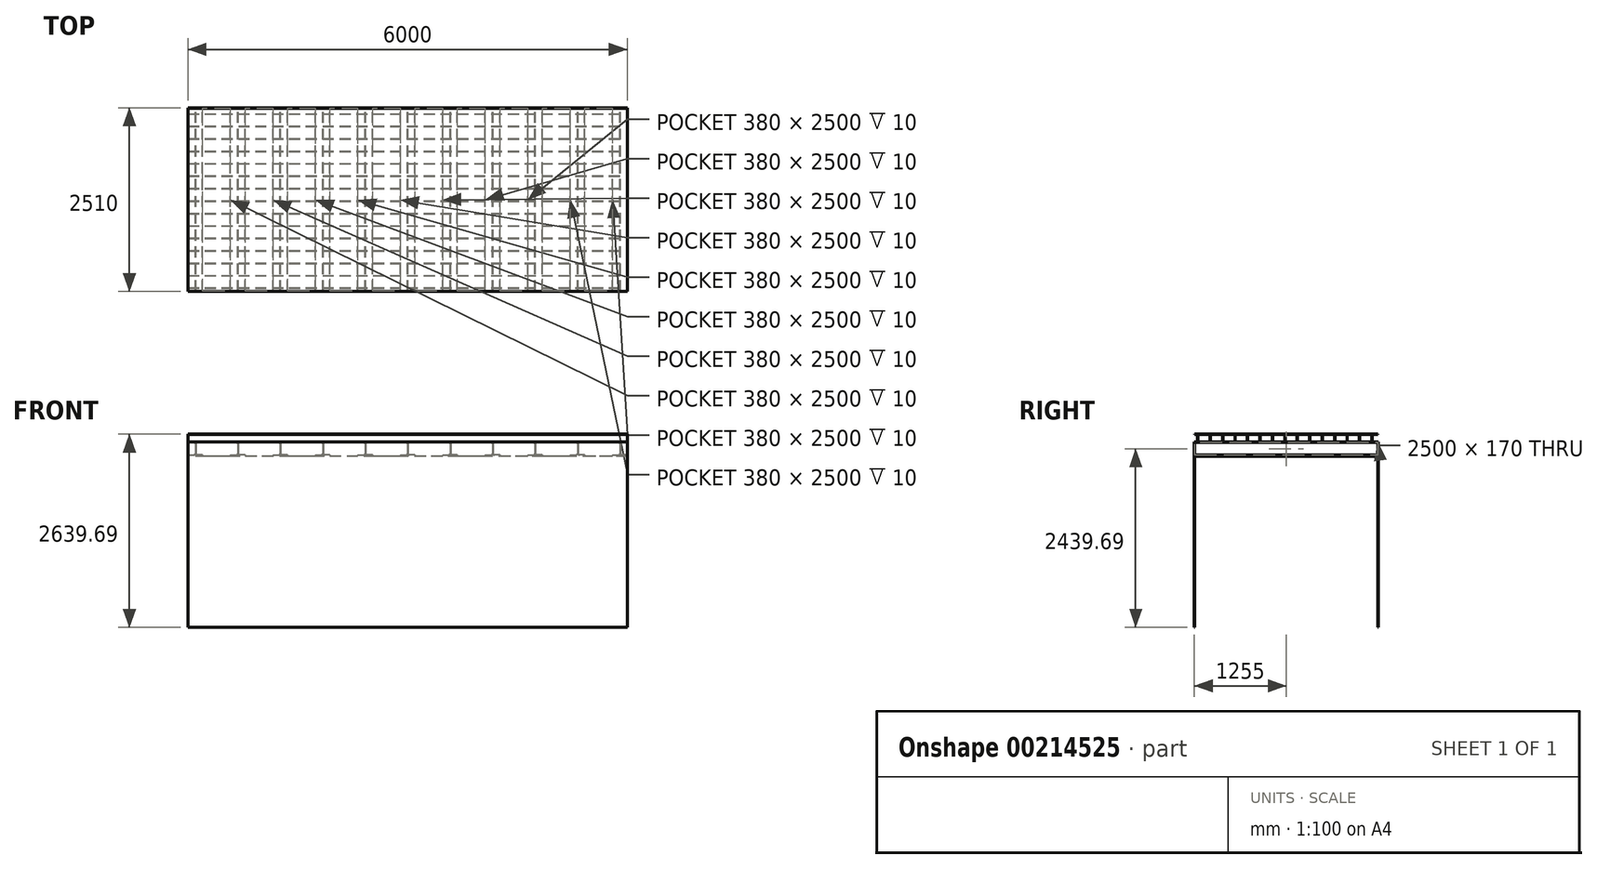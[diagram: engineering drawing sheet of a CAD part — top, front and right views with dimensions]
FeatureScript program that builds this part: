
annotation { "Feature Type Name" : "Feature", "Feature Type Description" : "" }
export const myFeature = defineFeature(function(context is Context, id is Id, definition is map)
    precondition{}
    {
        {
            var Q0;
            Q0=qCreatedBy(makeId("Front.planeOp"),FACE);
            var sketch = newSketch(context, id + "F0", { "sketchPlane" : qUnion([Q0])});
            skLineSegment(sketch, "E0", {"start": v(-410.3, 0) * mm, "end": v(5589.7, 0) * mm});
            skLineSegment(sketch, "E1", {"start": v(5589.7, 0) * mm, "end": v(5589.7, -10) * mm});
            skLineSegment(sketch, "E2", {"start": v(5589.7, -10) * mm, "end": v(-410.3, -10) * mm});
            skLineSegment(sketch, "E3", {"start": v(-410.3, -10) * mm, "end": v(-410.3, 0) * mm});
            skLineSegment(sketch, "E4.bottom", {"start": v(-410.3, 10) * mm, "end": v(-328.3, 10) * mm});
            skLineSegment(sketch, "E4.top", {"start": v(-410.3, 0) * mm, "end": v(-210.3, 0) * mm});
            skLineSegment(sketch, "E4.left", {"start": v(-410.3, 10) * mm, "end": v(-410.3, 0) * mm});
            skLineSegment(sketch, "E4.right", {"start": v(-210.3, 10) * mm, "end": v(-210.3, 0) * mm});
            skLineSegment(sketch, "E5.left", {"start": v(-310.3, 162) * mm, "end": v(-310.3, 28) * mm});
            skLineSegment(sketch, "E5.right", {"start": v(-303.8, 162) * mm, "end": v(-303.8, 28) * mm});
            skLineSegment(sketch, "E6.bottom", {"start": v(-285.8, 180) * mm, "end": v(-210.3, 180) * mm});
            skLineSegment(sketch, "E6.top", {"start": v(-410.3, 190) * mm, "end": v(-210.3, 190) * mm});
            skLineSegment(sketch, "E6.left", {"start": v(-410.3, 180) * mm, "end": v(-410.3, 190) * mm});
            skLineSegment(sketch, "E6.right", {"start": v(-210.3, 180) * mm, "end": v(-210.3, 190) * mm});
            skPoint(sketch, "E7.newPointA", {"position": v(-410.3, 180) * mm});
            skArc(sketch, "E7.filletArc", {"start": v(-285.8, 180) * mm, "mid": v(-298.54, 174.73) * mm, "end": v(-303.8, 162) * mm});
            skLineSegment(sketch, "E8", {"start": v(-410.3, 180) * mm, "end": v(-328.3, 180) * mm});
            skArc(sketch, "E9.filletArc", {"start": v(-310.3, 162) * mm, "mid": v(-315.58, 174.73) * mm, "end": v(-328.3, 180) * mm});
            skPoint(sketch, "E10.newPointA", {"position": v(-210.3, 10) * mm});
            skArc(sketch, "E10.filletArc", {"start": v(-328.3, 10) * mm, "mid": v(-315.58, 15.27) * mm, "end": v(-310.3, 28) * mm});
            skLineSegment(sketch, "E11", {"start": v(-210.3, 10) * mm, "end": v(-285.8, 10) * mm});
            skArc(sketch, "E12.filletArc", {"start": v(-303.8, 28) * mm, "mid": v(-298.54, 15.27) * mm, "end": v(-285.8, 10) * mm});
            skArc(sketch, "E13.1.0.0", {"start": v(276.2, 28) * mm, "mid": v(281.46, 15.27) * mm, "end": v(294.2, 10) * mm});
            skLineSegment(sketch, "E13.1.0.1", {"start": v(169.7, 10) * mm, "end": v(251.7, 10) * mm});
            skLineSegment(sketch, "E13.1.0.2", {"start": v(169.7, 190) * mm, "end": v(369.7, 190) * mm});
            skLineSegment(sketch, "E13.1.0.3", {"start": v(169.7, 180) * mm, "end": v(251.7, 180) * mm});
            skLineSegment(sketch, "E13.1.0.4", {"start": v(269.7, 162) * mm, "end": v(269.7, 28) * mm});
            skPoint(sketch, "E13.1.0.5", {"position": v(369.7, 10) * mm});
            skArc(sketch, "E13.1.0.6", {"start": v(294.2, 180) * mm, "mid": v(281.46, 174.73) * mm, "end": v(276.2, 162) * mm});
            skPoint(sketch, "E13.1.0.7", {"position": v(169.7, 180) * mm});
            skArc(sketch, "E13.1.0.8", {"start": v(251.7, 10) * mm, "mid": v(264.42, 15.27) * mm, "end": v(269.7, 28) * mm});
            skLineSegment(sketch, "E13.1.0.9", {"start": v(294.2, 180) * mm, "end": v(369.7, 180) * mm});
            skLineSegment(sketch, "E13.1.0.10", {"start": v(276.2, 162) * mm, "end": v(276.2, 28) * mm});
            skLineSegment(sketch, "E13.1.0.11", {"start": v(369.7, 10) * mm, "end": v(294.2, 10) * mm});
            skArc(sketch, "E13.1.0.12", {"start": v(269.7, 162) * mm, "mid": v(264.42, 174.73) * mm, "end": v(251.7, 180) * mm});
            skLineSegment(sketch, "E13.1.0.13", {"start": v(369.7, 180) * mm, "end": v(369.7, 190) * mm});
            skLineSegment(sketch, "E13.1.0.14", {"start": v(169.7, 180) * mm, "end": v(169.7, 190) * mm});
            skLineSegment(sketch, "E13.1.0.15", {"start": v(169.7, 10) * mm, "end": v(169.7, 0) * mm});
            skLineSegment(sketch, "E13.1.0.16", {"start": v(169.7, 0) * mm, "end": v(369.7, 0) * mm});
            skLineSegment(sketch, "E13.1.0.17", {"start": v(369.7, 10) * mm, "end": v(369.7, 0) * mm});
            skArc(sketch, "E13.2.0.0", {"start": v(856.2, 28) * mm, "mid": v(861.46, 15.27) * mm, "end": v(874.2, 10) * mm});
            skLineSegment(sketch, "E13.2.0.1", {"start": v(749.7, 10) * mm, "end": v(831.7, 10) * mm});
            skLineSegment(sketch, "E13.2.0.2", {"start": v(749.7, 190) * mm, "end": v(949.7, 190) * mm});
            skLineSegment(sketch, "E13.2.0.3", {"start": v(749.7, 180) * mm, "end": v(831.7, 180) * mm});
            skLineSegment(sketch, "E13.2.0.4", {"start": v(849.7, 162) * mm, "end": v(849.7, 28) * mm});
            skPoint(sketch, "E13.2.0.5", {"position": v(949.7, 10) * mm});
            skArc(sketch, "E13.2.0.6", {"start": v(874.2, 180) * mm, "mid": v(861.46, 174.73) * mm, "end": v(856.2, 162) * mm});
            skPoint(sketch, "E13.2.0.7", {"position": v(749.7, 180) * mm});
            skArc(sketch, "E13.2.0.8", {"start": v(831.7, 10) * mm, "mid": v(844.42, 15.27) * mm, "end": v(849.7, 28) * mm});
            skLineSegment(sketch, "E13.2.0.9", {"start": v(874.2, 180) * mm, "end": v(949.7, 180) * mm});
            skLineSegment(sketch, "E13.2.0.10", {"start": v(856.2, 162) * mm, "end": v(856.2, 28) * mm});
            skLineSegment(sketch, "E13.2.0.11", {"start": v(949.7, 10) * mm, "end": v(874.2, 10) * mm});
            skArc(sketch, "E13.2.0.12", {"start": v(849.7, 162) * mm, "mid": v(844.42, 174.73) * mm, "end": v(831.7, 180) * mm});
            skLineSegment(sketch, "E13.2.0.13", {"start": v(949.7, 180) * mm, "end": v(949.7, 190) * mm});
            skLineSegment(sketch, "E13.2.0.14", {"start": v(749.7, 180) * mm, "end": v(749.7, 190) * mm});
            skLineSegment(sketch, "E13.2.0.15", {"start": v(749.7, 10) * mm, "end": v(749.7, 0) * mm});
            skLineSegment(sketch, "E13.2.0.16", {"start": v(749.7, 0) * mm, "end": v(949.7, 0) * mm});
            skLineSegment(sketch, "E13.2.0.17", {"start": v(949.7, 10) * mm, "end": v(949.7, 0) * mm});
            skArc(sketch, "E13.3.0.0", {"start": v(1436.2, 28) * mm, "mid": v(1441.46, 15.27) * mm, "end": v(1454.2, 10) * mm});
            skLineSegment(sketch, "E13.3.0.1", {"start": v(1329.7, 10) * mm, "end": v(1411.7, 10) * mm});
            skLineSegment(sketch, "E13.3.0.2", {"start": v(1329.7, 190) * mm, "end": v(1529.7, 190) * mm});
            skLineSegment(sketch, "E13.3.0.3", {"start": v(1329.7, 180) * mm, "end": v(1411.7, 180) * mm});
            skLineSegment(sketch, "E13.3.0.4", {"start": v(1429.7, 162) * mm, "end": v(1429.7, 28) * mm});
            skPoint(sketch, "E13.3.0.5", {"position": v(1529.7, 10) * mm});
            skArc(sketch, "E13.3.0.6", {"start": v(1454.2, 180) * mm, "mid": v(1441.46, 174.73) * mm, "end": v(1436.2, 162) * mm});
            skPoint(sketch, "E13.3.0.7", {"position": v(1329.7, 180) * mm});
            skArc(sketch, "E13.3.0.8", {"start": v(1411.7, 10) * mm, "mid": v(1424.42, 15.27) * mm, "end": v(1429.7, 28) * mm});
            skLineSegment(sketch, "E13.3.0.9", {"start": v(1454.2, 180) * mm, "end": v(1529.7, 180) * mm});
            skLineSegment(sketch, "E13.3.0.10", {"start": v(1436.2, 162) * mm, "end": v(1436.2, 28) * mm});
            skLineSegment(sketch, "E13.3.0.11", {"start": v(1529.7, 10) * mm, "end": v(1454.2, 10) * mm});
            skArc(sketch, "E13.3.0.12", {"start": v(1429.7, 162) * mm, "mid": v(1424.42, 174.73) * mm, "end": v(1411.7, 180) * mm});
            skLineSegment(sketch, "E13.3.0.13", {"start": v(1529.7, 180) * mm, "end": v(1529.7, 190) * mm});
            skLineSegment(sketch, "E13.3.0.14", {"start": v(1329.7, 180) * mm, "end": v(1329.7, 190) * mm});
            skLineSegment(sketch, "E13.3.0.15", {"start": v(1329.7, 10) * mm, "end": v(1329.7, 0) * mm});
            skLineSegment(sketch, "E13.3.0.16", {"start": v(1329.7, 0) * mm, "end": v(1529.7, 0) * mm});
            skLineSegment(sketch, "E13.3.0.17", {"start": v(1529.7, 10) * mm, "end": v(1529.7, 0) * mm});
            skArc(sketch, "E13.4.0.0", {"start": v(2016.2, 28) * mm, "mid": v(2021.46, 15.27) * mm, "end": v(2034.2, 10) * mm});
            skLineSegment(sketch, "E13.4.0.1", {"start": v(1909.7, 10) * mm, "end": v(1991.7, 10) * mm});
            skLineSegment(sketch, "E13.4.0.2", {"start": v(1909.7, 190) * mm, "end": v(2109.7, 190) * mm});
            skLineSegment(sketch, "E13.4.0.3", {"start": v(1909.7, 180) * mm, "end": v(1991.7, 180) * mm});
            skLineSegment(sketch, "E13.4.0.4", {"start": v(2009.7, 162) * mm, "end": v(2009.7, 28) * mm});
            skPoint(sketch, "E13.4.0.5", {"position": v(2109.7, 10) * mm});
            skArc(sketch, "E13.4.0.6", {"start": v(2034.2, 180) * mm, "mid": v(2021.46, 174.73) * mm, "end": v(2016.2, 162) * mm});
            skPoint(sketch, "E13.4.0.7", {"position": v(1909.7, 180) * mm});
            skArc(sketch, "E13.4.0.8", {"start": v(1991.7, 10) * mm, "mid": v(2004.42, 15.27) * mm, "end": v(2009.7, 28) * mm});
            skLineSegment(sketch, "E13.4.0.9", {"start": v(2034.2, 180) * mm, "end": v(2109.7, 180) * mm});
            skLineSegment(sketch, "E13.4.0.10", {"start": v(2016.2, 162) * mm, "end": v(2016.2, 28) * mm});
            skLineSegment(sketch, "E13.4.0.11", {"start": v(2109.7, 10) * mm, "end": v(2034.2, 10) * mm});
            skArc(sketch, "E13.4.0.12", {"start": v(2009.7, 162) * mm, "mid": v(2004.42, 174.73) * mm, "end": v(1991.7, 180) * mm});
            skLineSegment(sketch, "E13.4.0.13", {"start": v(2109.7, 180) * mm, "end": v(2109.7, 190) * mm});
            skLineSegment(sketch, "E13.4.0.14", {"start": v(1909.7, 180) * mm, "end": v(1909.7, 190) * mm});
            skLineSegment(sketch, "E13.4.0.15", {"start": v(1909.7, 10) * mm, "end": v(1909.7, 0) * mm});
            skLineSegment(sketch, "E13.4.0.16", {"start": v(1909.7, 0) * mm, "end": v(2109.7, 0) * mm});
            skLineSegment(sketch, "E13.4.0.17", {"start": v(2109.7, 10) * mm, "end": v(2109.7, 0) * mm});
            skArc(sketch, "E13.5.0.0", {"start": v(2596.2, 28) * mm, "mid": v(2601.46, 15.27) * mm, "end": v(2614.2, 10) * mm});
            skLineSegment(sketch, "E13.5.0.1", {"start": v(2489.7, 10) * mm, "end": v(2571.7, 10) * mm});
            skLineSegment(sketch, "E13.5.0.2", {"start": v(2489.7, 190) * mm, "end": v(2689.7, 190) * mm});
            skLineSegment(sketch, "E13.5.0.3", {"start": v(2489.7, 180) * mm, "end": v(2571.7, 180) * mm});
            skLineSegment(sketch, "E13.5.0.4", {"start": v(2589.7, 162) * mm, "end": v(2589.7, 28) * mm});
            skPoint(sketch, "E13.5.0.5", {"position": v(2689.7, 10) * mm});
            skArc(sketch, "E13.5.0.6", {"start": v(2614.2, 180) * mm, "mid": v(2601.46, 174.73) * mm, "end": v(2596.2, 162) * mm});
            skPoint(sketch, "E13.5.0.7", {"position": v(2489.7, 180) * mm});
            skArc(sketch, "E13.5.0.8", {"start": v(2571.7, 10) * mm, "mid": v(2584.42, 15.27) * mm, "end": v(2589.7, 28) * mm});
            skLineSegment(sketch, "E13.5.0.9", {"start": v(2614.2, 180) * mm, "end": v(2689.7, 180) * mm});
            skLineSegment(sketch, "E13.5.0.10", {"start": v(2596.2, 162) * mm, "end": v(2596.2, 28) * mm});
            skLineSegment(sketch, "E13.5.0.11", {"start": v(2689.7, 10) * mm, "end": v(2614.2, 10) * mm});
            skArc(sketch, "E13.5.0.12", {"start": v(2589.7, 162) * mm, "mid": v(2584.42, 174.73) * mm, "end": v(2571.7, 180) * mm});
            skLineSegment(sketch, "E13.5.0.13", {"start": v(2689.7, 180) * mm, "end": v(2689.7, 190) * mm});
            skLineSegment(sketch, "E13.5.0.14", {"start": v(2489.7, 180) * mm, "end": v(2489.7, 190) * mm});
            skLineSegment(sketch, "E13.5.0.15", {"start": v(2489.7, 10) * mm, "end": v(2489.7, 0) * mm});
            skLineSegment(sketch, "E13.5.0.16", {"start": v(2489.7, 0) * mm, "end": v(2689.7, 0) * mm});
            skLineSegment(sketch, "E13.5.0.17", {"start": v(2689.7, 10) * mm, "end": v(2689.7, 0) * mm});
            skArc(sketch, "E13.6.0.0", {"start": v(3176.2, 28) * mm, "mid": v(3181.46, 15.27) * mm, "end": v(3194.2, 10) * mm});
            skLineSegment(sketch, "E13.6.0.1", {"start": v(3069.7, 10) * mm, "end": v(3151.7, 10) * mm});
            skLineSegment(sketch, "E13.6.0.2", {"start": v(3069.7, 190) * mm, "end": v(3269.7, 190) * mm});
            skLineSegment(sketch, "E13.6.0.3", {"start": v(3069.7, 180) * mm, "end": v(3151.7, 180) * mm});
            skLineSegment(sketch, "E13.6.0.4", {"start": v(3169.7, 162) * mm, "end": v(3169.7, 28) * mm});
            skPoint(sketch, "E13.6.0.5", {"position": v(3269.7, 10) * mm});
            skArc(sketch, "E13.6.0.6", {"start": v(3194.2, 180) * mm, "mid": v(3181.46, 174.73) * mm, "end": v(3176.2, 162) * mm});
            skPoint(sketch, "E13.6.0.7", {"position": v(3069.7, 180) * mm});
            skArc(sketch, "E13.6.0.8", {"start": v(3151.7, 10) * mm, "mid": v(3164.42, 15.27) * mm, "end": v(3169.7, 28) * mm});
            skLineSegment(sketch, "E13.6.0.9", {"start": v(3194.2, 180) * mm, "end": v(3269.7, 180) * mm});
            skLineSegment(sketch, "E13.6.0.10", {"start": v(3176.2, 162) * mm, "end": v(3176.2, 28) * mm});
            skLineSegment(sketch, "E13.6.0.11", {"start": v(3269.7, 10) * mm, "end": v(3194.2, 10) * mm});
            skArc(sketch, "E13.6.0.12", {"start": v(3169.7, 162) * mm, "mid": v(3164.42, 174.73) * mm, "end": v(3151.7, 180) * mm});
            skLineSegment(sketch, "E13.6.0.13", {"start": v(3269.7, 180) * mm, "end": v(3269.7, 190) * mm});
            skLineSegment(sketch, "E13.6.0.14", {"start": v(3069.7, 180) * mm, "end": v(3069.7, 190) * mm});
            skLineSegment(sketch, "E13.6.0.15", {"start": v(3069.7, 10) * mm, "end": v(3069.7, 0) * mm});
            skLineSegment(sketch, "E13.6.0.16", {"start": v(3069.7, 0) * mm, "end": v(3269.7, 0) * mm});
            skLineSegment(sketch, "E13.6.0.17", {"start": v(3269.7, 10) * mm, "end": v(3269.7, 0) * mm});
            skArc(sketch, "E13.7.0.0", {"start": v(3756.2, 28) * mm, "mid": v(3761.46, 15.27) * mm, "end": v(3774.2, 10) * mm});
            skLineSegment(sketch, "E13.7.0.1", {"start": v(3649.7, 10) * mm, "end": v(3731.7, 10) * mm});
            skLineSegment(sketch, "E13.7.0.2", {"start": v(3649.7, 190) * mm, "end": v(3849.7, 190) * mm});
            skLineSegment(sketch, "E13.7.0.3", {"start": v(3649.7, 180) * mm, "end": v(3731.7, 180) * mm});
            skLineSegment(sketch, "E13.7.0.4", {"start": v(3749.7, 162) * mm, "end": v(3749.7, 28) * mm});
            skPoint(sketch, "E13.7.0.5", {"position": v(3849.7, 10) * mm});
            skArc(sketch, "E13.7.0.6", {"start": v(3774.2, 180) * mm, "mid": v(3761.46, 174.73) * mm, "end": v(3756.2, 162) * mm});
            skPoint(sketch, "E13.7.0.7", {"position": v(3649.7, 180) * mm});
            skArc(sketch, "E13.7.0.8", {"start": v(3731.7, 10) * mm, "mid": v(3744.42, 15.27) * mm, "end": v(3749.7, 28) * mm});
            skLineSegment(sketch, "E13.7.0.9", {"start": v(3774.2, 180) * mm, "end": v(3849.7, 180) * mm});
            skLineSegment(sketch, "E13.7.0.10", {"start": v(3756.2, 162) * mm, "end": v(3756.2, 28) * mm});
            skLineSegment(sketch, "E13.7.0.11", {"start": v(3849.7, 10) * mm, "end": v(3774.2, 10) * mm});
            skArc(sketch, "E13.7.0.12", {"start": v(3749.7, 162) * mm, "mid": v(3744.42, 174.73) * mm, "end": v(3731.7, 180) * mm});
            skLineSegment(sketch, "E13.7.0.13", {"start": v(3849.7, 180) * mm, "end": v(3849.7, 190) * mm});
            skLineSegment(sketch, "E13.7.0.14", {"start": v(3649.7, 180) * mm, "end": v(3649.7, 190) * mm});
            skLineSegment(sketch, "E13.7.0.15", {"start": v(3649.7, 10) * mm, "end": v(3649.7, 0) * mm});
            skLineSegment(sketch, "E13.7.0.16", {"start": v(3649.7, 0) * mm, "end": v(3849.7, 0) * mm});
            skLineSegment(sketch, "E13.7.0.17", {"start": v(3849.7, 10) * mm, "end": v(3849.7, 0) * mm});
            skArc(sketch, "E13.8.0.0", {"start": v(4336.2, 28) * mm, "mid": v(4341.46, 15.27) * mm, "end": v(4354.2, 10) * mm});
            skLineSegment(sketch, "E13.8.0.1", {"start": v(4229.7, 10) * mm, "end": v(4311.7, 10) * mm});
            skLineSegment(sketch, "E13.8.0.2", {"start": v(4229.7, 190) * mm, "end": v(4429.7, 190) * mm});
            skLineSegment(sketch, "E13.8.0.3", {"start": v(4229.7, 180) * mm, "end": v(4311.7, 180) * mm});
            skLineSegment(sketch, "E13.8.0.4", {"start": v(4329.7, 162) * mm, "end": v(4329.7, 28) * mm});
            skPoint(sketch, "E13.8.0.5", {"position": v(4429.7, 10) * mm});
            skArc(sketch, "E13.8.0.6", {"start": v(4354.2, 180) * mm, "mid": v(4341.46, 174.73) * mm, "end": v(4336.2, 162) * mm});
            skPoint(sketch, "E13.8.0.7", {"position": v(4229.7, 180) * mm});
            skArc(sketch, "E13.8.0.8", {"start": v(4311.7, 10) * mm, "mid": v(4324.42, 15.27) * mm, "end": v(4329.7, 28) * mm});
            skLineSegment(sketch, "E13.8.0.9", {"start": v(4354.2, 180) * mm, "end": v(4429.7, 180) * mm});
            skLineSegment(sketch, "E13.8.0.10", {"start": v(4336.2, 162) * mm, "end": v(4336.2, 28) * mm});
            skLineSegment(sketch, "E13.8.0.11", {"start": v(4429.7, 10) * mm, "end": v(4354.2, 10) * mm});
            skArc(sketch, "E13.8.0.12", {"start": v(4329.7, 162) * mm, "mid": v(4324.42, 174.73) * mm, "end": v(4311.7, 180) * mm});
            skLineSegment(sketch, "E13.8.0.13", {"start": v(4429.7, 180) * mm, "end": v(4429.7, 190) * mm});
            skLineSegment(sketch, "E13.8.0.14", {"start": v(4229.7, 180) * mm, "end": v(4229.7, 190) * mm});
            skLineSegment(sketch, "E13.8.0.15", {"start": v(4229.7, 10) * mm, "end": v(4229.7, 0) * mm});
            skLineSegment(sketch, "E13.8.0.16", {"start": v(4229.7, 0) * mm, "end": v(4429.7, 0) * mm});
            skLineSegment(sketch, "E13.8.0.17", {"start": v(4429.7, 10) * mm, "end": v(4429.7, 0) * mm});
            skArc(sketch, "E13.9.0.0", {"start": v(4916.2, 28) * mm, "mid": v(4921.46, 15.27) * mm, "end": v(4934.2, 10) * mm});
            skLineSegment(sketch, "E13.9.0.1", {"start": v(4809.7, 10) * mm, "end": v(4891.7, 10) * mm});
            skLineSegment(sketch, "E13.9.0.2", {"start": v(4809.7, 190) * mm, "end": v(5009.7, 190) * mm});
            skLineSegment(sketch, "E13.9.0.3", {"start": v(4809.7, 180) * mm, "end": v(4891.7, 180) * mm});
            skLineSegment(sketch, "E13.9.0.4", {"start": v(4909.7, 162) * mm, "end": v(4909.7, 28) * mm});
            skPoint(sketch, "E13.9.0.5", {"position": v(5009.7, 10) * mm});
            skArc(sketch, "E13.9.0.6", {"start": v(4934.2, 180) * mm, "mid": v(4921.46, 174.73) * mm, "end": v(4916.2, 162) * mm});
            skPoint(sketch, "E13.9.0.7", {"position": v(4809.7, 180) * mm});
            skArc(sketch, "E13.9.0.8", {"start": v(4891.7, 10) * mm, "mid": v(4904.42, 15.27) * mm, "end": v(4909.7, 28) * mm});
            skLineSegment(sketch, "E13.9.0.9", {"start": v(4934.2, 180) * mm, "end": v(5009.7, 180) * mm});
            skLineSegment(sketch, "E13.9.0.10", {"start": v(4916.2, 162) * mm, "end": v(4916.2, 28) * mm});
            skLineSegment(sketch, "E13.9.0.11", {"start": v(5009.7, 10) * mm, "end": v(4934.2, 10) * mm});
            skArc(sketch, "E13.9.0.12", {"start": v(4909.7, 162) * mm, "mid": v(4904.42, 174.73) * mm, "end": v(4891.7, 180) * mm});
            skLineSegment(sketch, "E13.9.0.13", {"start": v(5009.7, 180) * mm, "end": v(5009.7, 190) * mm});
            skLineSegment(sketch, "E13.9.0.14", {"start": v(4809.7, 180) * mm, "end": v(4809.7, 190) * mm});
            skLineSegment(sketch, "E13.9.0.15", {"start": v(4809.7, 10) * mm, "end": v(4809.7, 0) * mm});
            skLineSegment(sketch, "E13.9.0.16", {"start": v(4809.7, 0) * mm, "end": v(5009.7, 0) * mm});
            skLineSegment(sketch, "E13.9.0.17", {"start": v(5009.7, 10) * mm, "end": v(5009.7, 0) * mm});
            skArc(sketch, "E13.10.0.0", {"start": v(5496.2, 28) * mm, "mid": v(5501.46, 15.27) * mm, "end": v(5514.2, 10) * mm});
            skLineSegment(sketch, "E13.10.0.1", {"start": v(5389.7, 10) * mm, "end": v(5471.7, 10) * mm});
            skLineSegment(sketch, "E13.10.0.2", {"start": v(5389.7, 190) * mm, "end": v(5589.7, 190) * mm});
            skLineSegment(sketch, "E13.10.0.3", {"start": v(5389.7, 180) * mm, "end": v(5471.7, 180) * mm});
            skLineSegment(sketch, "E13.10.0.4", {"start": v(5489.7, 162) * mm, "end": v(5489.7, 28) * mm});
            skPoint(sketch, "E13.10.0.5", {"position": v(5589.7, 10) * mm});
            skArc(sketch, "E13.10.0.6", {"start": v(5514.2, 180) * mm, "mid": v(5501.46, 174.73) * mm, "end": v(5496.2, 162) * mm});
            skPoint(sketch, "E13.10.0.7", {"position": v(5389.7, 180) * mm});
            skArc(sketch, "E13.10.0.8", {"start": v(5471.7, 10) * mm, "mid": v(5484.42, 15.27) * mm, "end": v(5489.7, 28) * mm});
            skLineSegment(sketch, "E13.10.0.9", {"start": v(5514.2, 180) * mm, "end": v(5589.7, 180) * mm});
            skLineSegment(sketch, "E13.10.0.10", {"start": v(5496.2, 162) * mm, "end": v(5496.2, 28) * mm});
            skLineSegment(sketch, "E13.10.0.11", {"start": v(5589.7, 10) * mm, "end": v(5514.2, 10) * mm});
            skArc(sketch, "E13.10.0.12", {"start": v(5489.7, 162) * mm, "mid": v(5484.42, 174.73) * mm, "end": v(5471.7, 180) * mm});
            skLineSegment(sketch, "E13.10.0.13", {"start": v(5589.7, 180) * mm, "end": v(5589.7, 190) * mm});
            skLineSegment(sketch, "E13.10.0.14", {"start": v(5389.7, 180) * mm, "end": v(5389.7, 190) * mm});
            skLineSegment(sketch, "E13.10.0.15", {"start": v(5389.7, 10) * mm, "end": v(5389.7, 0) * mm});
            skLineSegment(sketch, "E13.10.0.16", {"start": v(5389.7, 0) * mm, "end": v(5589.7, 0) * mm});
            skLineSegment(sketch, "E13.10.0.17", {"start": v(5589.7, 10) * mm, "end": v(5589.7, 0) * mm});
            skLineSegment(sketch, "E13.direction1", {"start": v(-410.3, 0) * mm, "end": v(169.7, 0) * mm, "construction": true});
            skSolve(sketch);
        }
        {
            var Q0;
            Q0 = qSketchRegion(id + "F0", true);
            extrude(context, id + "F1", {"entities" : qUnion([Q0]), "depth" : 2500 * mm});
        }
        {
            var Q0;
            Q0=makeQuery(id+"F1.opExtrude","CAP_FACE",FACE,{"disambiguationData":[OSD([sQuery(id+"F0.wireOp",EDGE,"E0"),sQuery(id+"F0.wireOp",EDGE,"E1"),sQuery(id+"F0.wireOp",EDGE,"E2"),sQuery(id+"F0.wireOp",EDGE,"E3"),sQuery(id+"F0.wireOp",EDGE,"E4.bottom"),sQuery(id+"F0.wireOp",EDGE,"E4.left"),sQuery(id+"F0.wireOp",EDGE,"E4.right"),sQuery(id+"F0.wireOp",EDGE,"E5.left"),sQuery(id+"F0.wireOp",EDGE,"E5.right"),sQuery(id+"F0.wireOp",EDGE,"E6.bottom"),sQuery(id+"F0.wireOp",EDGE,"E6.top"),sQuery(id+"F0.wireOp",EDGE,"E6.left"),sQuery(id+"F0.wireOp",EDGE,"E6.right"),sQuery(id+"F0.wireOp",EDGE,"E7.filletArc"),sQuery(id+"F0.wireOp",EDGE,"E8"),sQuery(id+"F0.wireOp",EDGE,"E9.filletArc"),sQuery(id+"F0.wireOp",EDGE,"E10.filletArc"),sQuery(id+"F0.wireOp",EDGE,"E11"),sQuery(id+"F0.wireOp",EDGE,"E12.filletArc"),sQuery(id+"F0.wireOp",EDGE,"E13.1.0.0"),sQuery(id+"F0.wireOp",EDGE,"E13.1.0.1"),sQuery(id+"F0.wireOp",EDGE,"E13.1.0.2"),sQuery(id+"F0.wireOp",EDGE,"E13.1.0.3"),sQuery(id+"F0.wireOp",EDGE,"E13.1.0.4"),sQuery(id+"F0.wireOp",EDGE,"E13.1.0.6"),sQuery(id+"F0.wireOp",EDGE,"E13.1.0.8"),sQuery(id+"F0.wireOp",EDGE,"E13.1.0.9"),sQuery(id+"F0.wireOp",EDGE,"E13.1.0.10"),sQuery(id+"F0.wireOp",EDGE,"E13.1.0.11"),sQuery(id+"F0.wireOp",EDGE,"E13.1.0.12"),sQuery(id+"F0.wireOp",EDGE,"E13.1.0.13"),sQuery(id+"F0.wireOp",EDGE,"E13.1.0.14"),sQuery(id+"F0.wireOp",EDGE,"E13.1.0.15"),sQuery(id+"F0.wireOp",EDGE,"E13.1.0.17"),sQuery(id+"F0.wireOp",EDGE,"E13.2.0.0"),sQuery(id+"F0.wireOp",EDGE,"E13.2.0.1"),sQuery(id+"F0.wireOp",EDGE,"E13.2.0.2"),sQuery(id+"F0.wireOp",EDGE,"E13.2.0.3"),sQuery(id+"F0.wireOp",EDGE,"E13.2.0.4"),sQuery(id+"F0.wireOp",EDGE,"E13.2.0.6"),sQuery(id+"F0.wireOp",EDGE,"E13.2.0.8"),sQuery(id+"F0.wireOp",EDGE,"E13.2.0.9"),sQuery(id+"F0.wireOp",EDGE,"E13.2.0.10"),sQuery(id+"F0.wireOp",EDGE,"E13.2.0.11"),sQuery(id+"F0.wireOp",EDGE,"E13.2.0.12"),sQuery(id+"F0.wireOp",EDGE,"E13.2.0.13"),sQuery(id+"F0.wireOp",EDGE,"E13.2.0.14"),sQuery(id+"F0.wireOp",EDGE,"E13.2.0.15"),sQuery(id+"F0.wireOp",EDGE,"E13.2.0.17"),sQuery(id+"F0.wireOp",EDGE,"E13.3.0.0"),sQuery(id+"F0.wireOp",EDGE,"E13.3.0.1"),sQuery(id+"F0.wireOp",EDGE,"E13.3.0.2"),sQuery(id+"F0.wireOp",EDGE,"E13.3.0.3"),sQuery(id+"F0.wireOp",EDGE,"E13.3.0.4"),sQuery(id+"F0.wireOp",EDGE,"E13.3.0.6"),sQuery(id+"F0.wireOp",EDGE,"E13.3.0.8"),sQuery(id+"F0.wireOp",EDGE,"E13.3.0.9"),sQuery(id+"F0.wireOp",EDGE,"E13.3.0.10"),sQuery(id+"F0.wireOp",EDGE,"E13.3.0.11"),sQuery(id+"F0.wireOp",EDGE,"E13.3.0.12"),sQuery(id+"F0.wireOp",EDGE,"E13.3.0.13"),sQuery(id+"F0.wireOp",EDGE,"E13.3.0.14"),sQuery(id+"F0.wireOp",EDGE,"E13.3.0.15"),sQuery(id+"F0.wireOp",EDGE,"E13.3.0.17"),sQuery(id+"F0.wireOp",EDGE,"E13.4.0.0"),sQuery(id+"F0.wireOp",EDGE,"E13.4.0.1"),sQuery(id+"F0.wireOp",EDGE,"E13.4.0.2"),sQuery(id+"F0.wireOp",EDGE,"E13.4.0.3"),sQuery(id+"F0.wireOp",EDGE,"E13.4.0.4"),sQuery(id+"F0.wireOp",EDGE,"E13.4.0.6"),sQuery(id+"F0.wireOp",EDGE,"E13.4.0.8"),sQuery(id+"F0.wireOp",EDGE,"E13.4.0.9"),sQuery(id+"F0.wireOp",EDGE,"E13.4.0.10"),sQuery(id+"F0.wireOp",EDGE,"E13.4.0.11"),sQuery(id+"F0.wireOp",EDGE,"E13.4.0.12"),sQuery(id+"F0.wireOp",EDGE,"E13.4.0.13"),sQuery(id+"F0.wireOp",EDGE,"E13.4.0.14"),sQuery(id+"F0.wireOp",EDGE,"E13.4.0.15"),sQuery(id+"F0.wireOp",EDGE,"E13.4.0.17"),sQuery(id+"F0.wireOp",EDGE,"E13.5.0.0"),sQuery(id+"F0.wireOp",EDGE,"E13.5.0.1"),sQuery(id+"F0.wireOp",EDGE,"E13.5.0.2"),sQuery(id+"F0.wireOp",EDGE,"E13.5.0.3"),sQuery(id+"F0.wireOp",EDGE,"E13.5.0.4"),sQuery(id+"F0.wireOp",EDGE,"E13.5.0.6"),sQuery(id+"F0.wireOp",EDGE,"E13.5.0.8"),sQuery(id+"F0.wireOp",EDGE,"E13.5.0.9"),sQuery(id+"F0.wireOp",EDGE,"E13.5.0.10"),sQuery(id+"F0.wireOp",EDGE,"E13.5.0.11"),sQuery(id+"F0.wireOp",EDGE,"E13.5.0.12"),sQuery(id+"F0.wireOp",EDGE,"E13.5.0.13"),sQuery(id+"F0.wireOp",EDGE,"E13.5.0.14"),sQuery(id+"F0.wireOp",EDGE,"E13.5.0.15"),sQuery(id+"F0.wireOp",EDGE,"E13.5.0.17"),sQuery(id+"F0.wireOp",EDGE,"E13.6.0.0"),sQuery(id+"F0.wireOp",EDGE,"E13.6.0.1"),sQuery(id+"F0.wireOp",EDGE,"E13.6.0.2"),sQuery(id+"F0.wireOp",EDGE,"E13.6.0.3"),sQuery(id+"F0.wireOp",EDGE,"E13.6.0.4"),sQuery(id+"F0.wireOp",EDGE,"E13.6.0.6"),sQuery(id+"F0.wireOp",EDGE,"E13.6.0.8"),sQuery(id+"F0.wireOp",EDGE,"E13.6.0.9"),sQuery(id+"F0.wireOp",EDGE,"E13.6.0.10"),sQuery(id+"F0.wireOp",EDGE,"E13.6.0.11"),sQuery(id+"F0.wireOp",EDGE,"E13.6.0.12"),sQuery(id+"F0.wireOp",EDGE,"E13.6.0.13"),sQuery(id+"F0.wireOp",EDGE,"E13.6.0.14"),sQuery(id+"F0.wireOp",EDGE,"E13.6.0.15"),sQuery(id+"F0.wireOp",EDGE,"E13.6.0.17"),sQuery(id+"F0.wireOp",EDGE,"E13.7.0.0"),sQuery(id+"F0.wireOp",EDGE,"E13.7.0.1"),sQuery(id+"F0.wireOp",EDGE,"E13.7.0.2"),sQuery(id+"F0.wireOp",EDGE,"E13.7.0.3"),sQuery(id+"F0.wireOp",EDGE,"E13.7.0.4"),sQuery(id+"F0.wireOp",EDGE,"E13.7.0.6"),sQuery(id+"F0.wireOp",EDGE,"E13.7.0.8"),sQuery(id+"F0.wireOp",EDGE,"E13.7.0.9"),sQuery(id+"F0.wireOp",EDGE,"E13.7.0.10"),sQuery(id+"F0.wireOp",EDGE,"E13.7.0.11"),sQuery(id+"F0.wireOp",EDGE,"E13.7.0.12"),sQuery(id+"F0.wireOp",EDGE,"E13.7.0.13"),sQuery(id+"F0.wireOp",EDGE,"E13.7.0.14"),sQuery(id+"F0.wireOp",EDGE,"E13.7.0.15"),sQuery(id+"F0.wireOp",EDGE,"E13.7.0.17"),sQuery(id+"F0.wireOp",EDGE,"E13.8.0.0"),sQuery(id+"F0.wireOp",EDGE,"E13.8.0.1"),sQuery(id+"F0.wireOp",EDGE,"E13.8.0.2"),sQuery(id+"F0.wireOp",EDGE,"E13.8.0.3"),sQuery(id+"F0.wireOp",EDGE,"E13.8.0.4"),sQuery(id+"F0.wireOp",EDGE,"E13.8.0.6"),sQuery(id+"F0.wireOp",EDGE,"E13.8.0.8"),sQuery(id+"F0.wireOp",EDGE,"E13.8.0.9"),sQuery(id+"F0.wireOp",EDGE,"E13.8.0.10"),sQuery(id+"F0.wireOp",EDGE,"E13.8.0.11"),sQuery(id+"F0.wireOp",EDGE,"E13.8.0.12"),sQuery(id+"F0.wireOp",EDGE,"E13.8.0.13"),sQuery(id+"F0.wireOp",EDGE,"E13.8.0.14"),sQuery(id+"F0.wireOp",EDGE,"E13.8.0.15"),sQuery(id+"F0.wireOp",EDGE,"E13.8.0.17"),sQuery(id+"F0.wireOp",EDGE,"E13.9.0.0"),sQuery(id+"F0.wireOp",EDGE,"E13.9.0.1"),sQuery(id+"F0.wireOp",EDGE,"E13.9.0.2"),sQuery(id+"F0.wireOp",EDGE,"E13.9.0.3"),sQuery(id+"F0.wireOp",EDGE,"E13.9.0.4"),sQuery(id+"F0.wireOp",EDGE,"E13.9.0.6"),sQuery(id+"F0.wireOp",EDGE,"E13.9.0.8"),sQuery(id+"F0.wireOp",EDGE,"E13.9.0.9"),sQuery(id+"F0.wireOp",EDGE,"E13.9.0.10"),sQuery(id+"F0.wireOp",EDGE,"E13.9.0.11"),sQuery(id+"F0.wireOp",EDGE,"E13.9.0.12"),sQuery(id+"F0.wireOp",EDGE,"E13.9.0.13"),sQuery(id+"F0.wireOp",EDGE,"E13.9.0.14"),sQuery(id+"F0.wireOp",EDGE,"E13.9.0.15"),sQuery(id+"F0.wireOp",EDGE,"E13.9.0.17"),sQuery(id+"F0.wireOp",EDGE,"E13.10.0.0"),sQuery(id+"F0.wireOp",EDGE,"E13.10.0.1"),sQuery(id+"F0.wireOp",EDGE,"E13.10.0.2"),sQuery(id+"F0.wireOp",EDGE,"E13.10.0.3"),sQuery(id+"F0.wireOp",EDGE,"E13.10.0.4"),sQuery(id+"F0.wireOp",EDGE,"E13.10.0.6"),sQuery(id+"F0.wireOp",EDGE,"E13.10.0.8"),sQuery(id+"F0.wireOp",EDGE,"E13.10.0.9"),sQuery(id+"F0.wireOp",EDGE,"E13.10.0.10"),sQuery(id+"F0.wireOp",EDGE,"E13.10.0.11"),sQuery(id+"F0.wireOp",EDGE,"E13.10.0.12"),sQuery(id+"F0.wireOp",EDGE,"E13.10.0.13"),sQuery(id+"F0.wireOp",EDGE,"E13.10.0.14"),sQuery(id+"F0.wireOp",EDGE,"E13.10.0.15"),sQuery(id+"F0.wireOp",EDGE,"E13.10.0.17"),sQuery(id+"F0.wireOp",EDGE,"E13.11.0.0"),sQuery(id+"F0.wireOp",EDGE,"E13.11.0.1"),sQuery(id+"F0.wireOp",EDGE,"E13.11.0.2"),sQuery(id+"F0.wireOp",EDGE,"E13.11.0.3"),sQuery(id+"F0.wireOp",EDGE,"E13.11.0.4"),sQuery(id+"F0.wireOp",EDGE,"E13.11.0.6"),sQuery(id+"F0.wireOp",EDGE,"E13.11.0.8"),sQuery(id+"F0.wireOp",EDGE,"E13.11.0.9"),sQuery(id+"F0.wireOp",EDGE,"E13.11.0.10"),sQuery(id+"F0.wireOp",EDGE,"E13.11.0.11"),sQuery(id+"F0.wireOp",EDGE,"E13.11.0.12"),sQuery(id+"F0.wireOp",EDGE,"E13.11.0.13"),sQuery(id+"F0.wireOp",EDGE,"E13.11.0.14"),sQuery(id+"F0.wireOp",EDGE,"E13.11.0.15"),sQuery(id+"F0.wireOp",EDGE,"E13.11.0.17"),sQuery(id+"F0.wireOp",EDGE,"E13.12.0.0"),sQuery(id+"F0.wireOp",EDGE,"E13.12.0.1"),sQuery(id+"F0.wireOp",EDGE,"E13.12.0.2"),sQuery(id+"F0.wireOp",EDGE,"E13.12.0.3"),sQuery(id+"F0.wireOp",EDGE,"E13.12.0.4"),sQuery(id+"F0.wireOp",EDGE,"E13.12.0.6"),sQuery(id+"F0.wireOp",EDGE,"E13.12.0.8"),sQuery(id+"F0.wireOp",EDGE,"E13.12.0.9"),sQuery(id+"F0.wireOp",EDGE,"E13.12.0.10"),sQuery(id+"F0.wireOp",EDGE,"E13.12.0.11"),sQuery(id+"F0.wireOp",EDGE,"E13.12.0.12"),sQuery(id+"F0.wireOp",EDGE,"E13.12.0.13"),sQuery(id+"F0.wireOp",EDGE,"E13.12.0.14"),sQuery(id+"F0.wireOp",EDGE,"E13.12.0.15"),sQuery(id+"F0.wireOp",EDGE,"E13.12.0.17"),sQuery(id+"F0.wireOp",EDGE,"E13.13.0.0"),sQuery(id+"F0.wireOp",EDGE,"E13.13.0.1"),sQuery(id+"F0.wireOp",EDGE,"E13.13.0.2"),sQuery(id+"F0.wireOp",EDGE,"E13.13.0.3"),sQuery(id+"F0.wireOp",EDGE,"E13.13.0.4"),sQuery(id+"F0.wireOp",EDGE,"E13.13.0.6"),sQuery(id+"F0.wireOp",EDGE,"E13.13.0.8"),sQuery(id+"F0.wireOp",EDGE,"E13.13.0.9"),sQuery(id+"F0.wireOp",EDGE,"E13.13.0.10"),sQuery(id+"F0.wireOp",EDGE,"E13.13.0.11"),sQuery(id+"F0.wireOp",EDGE,"E13.13.0.12"),sQuery(id+"F0.wireOp",EDGE,"E13.13.0.13"),sQuery(id+"F0.wireOp",EDGE,"E13.13.0.14"),sQuery(id+"F0.wireOp",EDGE,"E13.13.0.15"),sQuery(id+"F0.wireOp",EDGE,"E13.13.0.17"),sQuery(id+"F0.wireOp",EDGE,"E13.14.0.0"),sQuery(id+"F0.wireOp",EDGE,"E13.14.0.1"),sQuery(id+"F0.wireOp",EDGE,"E13.14.0.2"),sQuery(id+"F0.wireOp",EDGE,"E13.14.0.3"),sQuery(id+"F0.wireOp",EDGE,"E13.14.0.4"),sQuery(id+"F0.wireOp",EDGE,"E13.14.0.6"),sQuery(id+"F0.wireOp",EDGE,"E13.14.0.8"),sQuery(id+"F0.wireOp",EDGE,"E13.14.0.9"),sQuery(id+"F0.wireOp",EDGE,"E13.14.0.10"),sQuery(id+"F0.wireOp",EDGE,"E13.14.0.11"),sQuery(id+"F0.wireOp",EDGE,"E13.14.0.12"),sQuery(id+"F0.wireOp",EDGE,"E13.14.0.13"),sQuery(id+"F0.wireOp",EDGE,"E13.14.0.14"),sQuery(id+"F0.wireOp",EDGE,"E13.14.0.15"),sQuery(id+"F0.wireOp",EDGE,"E13.14.0.17"),sQuery(id+"F0.wireOp",EDGE,"E13.15.0.0"),sQuery(id+"F0.wireOp",EDGE,"E13.15.0.1"),sQuery(id+"F0.wireOp",EDGE,"E13.15.0.2"),sQuery(id+"F0.wireOp",EDGE,"E13.15.0.3"),sQuery(id+"F0.wireOp",EDGE,"E13.15.0.4"),sQuery(id+"F0.wireOp",EDGE,"E13.15.0.6"),sQuery(id+"F0.wireOp",EDGE,"E13.15.0.8"),sQuery(id+"F0.wireOp",EDGE,"E13.15.0.9"),sQuery(id+"F0.wireOp",EDGE,"E13.15.0.10"),sQuery(id+"F0.wireOp",EDGE,"E13.15.0.11"),sQuery(id+"F0.wireOp",EDGE,"E13.15.0.12"),sQuery(id+"F0.wireOp",EDGE,"E13.15.0.13"),sQuery(id+"F0.wireOp",EDGE,"E13.15.0.14"),sQuery(id+"F0.wireOp",EDGE,"E13.15.0.15"),sQuery(id+"F0.wireOp",EDGE,"E13.15.0.17"),sQuery(id+"F0.wireOp",EDGE,"E13.16.0.0"),sQuery(id+"F0.wireOp",EDGE,"E13.16.0.1"),sQuery(id+"F0.wireOp",EDGE,"E13.16.0.2"),sQuery(id+"F0.wireOp",EDGE,"E13.16.0.3"),sQuery(id+"F0.wireOp",EDGE,"E13.16.0.4"),sQuery(id+"F0.wireOp",EDGE,"E13.16.0.6"),sQuery(id+"F0.wireOp",EDGE,"E13.16.0.8"),sQuery(id+"F0.wireOp",EDGE,"E13.16.0.9"),sQuery(id+"F0.wireOp",EDGE,"E13.16.0.10"),sQuery(id+"F0.wireOp",EDGE,"E13.16.0.11"),sQuery(id+"F0.wireOp",EDGE,"E13.16.0.12"),sQuery(id+"F0.wireOp",EDGE,"E13.16.0.13"),sQuery(id+"F0.wireOp",EDGE,"E13.16.0.14"),sQuery(id+"F0.wireOp",EDGE,"E13.16.0.15"),sQuery(id+"F0.wireOp",EDGE,"E13.16.0.17"),sQuery(id+"F0.wireOp",EDGE,"E13.17.0.0"),sQuery(id+"F0.wireOp",EDGE,"E13.17.0.1"),sQuery(id+"F0.wireOp",EDGE,"E13.17.0.2"),sQuery(id+"F0.wireOp",EDGE,"E13.17.0.3"),sQuery(id+"F0.wireOp",EDGE,"E13.17.0.4"),sQuery(id+"F0.wireOp",EDGE,"E13.17.0.6"),sQuery(id+"F0.wireOp",EDGE,"E13.17.0.8"),sQuery(id+"F0.wireOp",EDGE,"E13.17.0.9"),sQuery(id+"F0.wireOp",EDGE,"E13.17.0.10"),sQuery(id+"F0.wireOp",EDGE,"E13.17.0.11"),sQuery(id+"F0.wireOp",EDGE,"E13.17.0.12"),sQuery(id+"F0.wireOp",EDGE,"E13.17.0.13"),sQuery(id+"F0.wireOp",EDGE,"E13.17.0.14"),sQuery(id+"F0.wireOp",EDGE,"E13.17.0.15"),sQuery(id+"F0.wireOp",EDGE,"E13.17.0.17"),sQuery(id+"F0.wireOp",EDGE,"E13.18.0.0"),sQuery(id+"F0.wireOp",EDGE,"E13.18.0.1"),sQuery(id+"F0.wireOp",EDGE,"E13.18.0.2"),sQuery(id+"F0.wireOp",EDGE,"E13.18.0.3"),sQuery(id+"F0.wireOp",EDGE,"E13.18.0.4"),sQuery(id+"F0.wireOp",EDGE,"E13.18.0.6"),sQuery(id+"F0.wireOp",EDGE,"E13.18.0.8"),sQuery(id+"F0.wireOp",EDGE,"E13.18.0.9"),sQuery(id+"F0.wireOp",EDGE,"E13.18.0.10"),sQuery(id+"F0.wireOp",EDGE,"E13.18.0.11"),sQuery(id+"F0.wireOp",EDGE,"E13.18.0.12"),sQuery(id+"F0.wireOp",EDGE,"E13.18.0.13"),sQuery(id+"F0.wireOp",EDGE,"E13.18.0.14"),sQuery(id+"F0.wireOp",EDGE,"E13.18.0.15"),sQuery(id+"F0.wireOp",EDGE,"E13.18.0.17"),sQuery(id+"F0.wireOp",EDGE,"E13.19.0.0"),sQuery(id+"F0.wireOp",EDGE,"E13.19.0.1"),sQuery(id+"F0.wireOp",EDGE,"E13.19.0.2"),sQuery(id+"F0.wireOp",EDGE,"E13.19.0.3"),sQuery(id+"F0.wireOp",EDGE,"E13.19.0.4"),sQuery(id+"F0.wireOp",EDGE,"E13.19.0.6"),sQuery(id+"F0.wireOp",EDGE,"E13.19.0.8"),sQuery(id+"F0.wireOp",EDGE,"E13.19.0.9"),sQuery(id+"F0.wireOp",EDGE,"E13.19.0.10"),sQuery(id+"F0.wireOp",EDGE,"E13.19.0.11"),sQuery(id+"F0.wireOp",EDGE,"E13.19.0.12"),sQuery(id+"F0.wireOp",EDGE,"E13.19.0.13"),sQuery(id+"F0.wireOp",EDGE,"E13.19.0.14"),sQuery(id+"F0.wireOp",EDGE,"E13.19.0.15"),sQuery(id+"F0.wireOp",EDGE,"E13.19.0.17"),sQuery(id+"F0.wireOp",EDGE,"E13.20.0.0"),sQuery(id+"F0.wireOp",EDGE,"E13.20.0.1"),sQuery(id+"F0.wireOp",EDGE,"E13.20.0.2"),sQuery(id+"F0.wireOp",EDGE,"E13.20.0.3"),sQuery(id+"F0.wireOp",EDGE,"E13.20.0.4"),sQuery(id+"F0.wireOp",EDGE,"E13.20.0.6"),sQuery(id+"F0.wireOp",EDGE,"E13.20.0.8"),sQuery(id+"F0.wireOp",EDGE,"E13.20.0.9"),sQuery(id+"F0.wireOp",EDGE,"E13.20.0.10"),sQuery(id+"F0.wireOp",EDGE,"E13.20.0.11"),sQuery(id+"F0.wireOp",EDGE,"E13.20.0.12"),sQuery(id+"F0.wireOp",EDGE,"E13.20.0.13"),sQuery(id+"F0.wireOp",EDGE,"E13.20.0.14"),sQuery(id+"F0.wireOp",EDGE,"E13.20.0.15"),sQuery(id+"F0.wireOp",EDGE,"E13.20.0.17"),sQuery(id+"F0.wireOp",EDGE,"E13.21.0.0"),sQuery(id+"F0.wireOp",EDGE,"E13.21.0.1"),sQuery(id+"F0.wireOp",EDGE,"E13.21.0.2"),sQuery(id+"F0.wireOp",EDGE,"E13.21.0.3"),sQuery(id+"F0.wireOp",EDGE,"E13.21.0.4"),sQuery(id+"F0.wireOp",EDGE,"E13.21.0.6"),sQuery(id+"F0.wireOp",EDGE,"E13.21.0.8"),sQuery(id+"F0.wireOp",EDGE,"E13.21.0.9"),sQuery(id+"F0.wireOp",EDGE,"E13.21.0.10"),sQuery(id+"F0.wireOp",EDGE,"E13.21.0.11"),sQuery(id+"F0.wireOp",EDGE,"E13.21.0.12"),sQuery(id+"F0.wireOp",EDGE,"E13.21.0.13"),sQuery(id+"F0.wireOp",EDGE,"E13.21.0.14"),sQuery(id+"F0.wireOp",EDGE,"E13.21.0.15"),sQuery(id+"F0.wireOp",EDGE,"E13.21.0.17"),sQuery(id+"F0.wireOp",EDGE,"E13.22.0.0"),sQuery(id+"F0.wireOp",EDGE,"E13.22.0.1"),sQuery(id+"F0.wireOp",EDGE,"E13.22.0.2"),sQuery(id+"F0.wireOp",EDGE,"E13.22.0.3"),sQuery(id+"F0.wireOp",EDGE,"E13.22.0.4"),sQuery(id+"F0.wireOp",EDGE,"E13.22.0.6"),sQuery(id+"F0.wireOp",EDGE,"E13.22.0.8"),sQuery(id+"F0.wireOp",EDGE,"E13.22.0.9"),sQuery(id+"F0.wireOp",EDGE,"E13.22.0.10"),sQuery(id+"F0.wireOp",EDGE,"E13.22.0.11"),sQuery(id+"F0.wireOp",EDGE,"E13.22.0.12"),sQuery(id+"F0.wireOp",EDGE,"E13.22.0.13"),sQuery(id+"F0.wireOp",EDGE,"E13.22.0.14"),sQuery(id+"F0.wireOp",EDGE,"E13.22.0.15"),sQuery(id+"F0.wireOp",EDGE,"E13.22.0.17"),sQuery(id+"F0.wireOp",EDGE,"E13.23.0.0"),sQuery(id+"F0.wireOp",EDGE,"E13.23.0.1"),sQuery(id+"F0.wireOp",EDGE,"E13.23.0.2"),sQuery(id+"F0.wireOp",EDGE,"E13.23.0.3"),sQuery(id+"F0.wireOp",EDGE,"E13.23.0.4"),sQuery(id+"F0.wireOp",EDGE,"E13.23.0.6"),sQuery(id+"F0.wireOp",EDGE,"E13.23.0.8"),sQuery(id+"F0.wireOp",EDGE,"E13.23.0.9"),sQuery(id+"F0.wireOp",EDGE,"E13.23.0.10"),sQuery(id+"F0.wireOp",EDGE,"E13.23.0.11"),sQuery(id+"F0.wireOp",EDGE,"E13.23.0.12"),sQuery(id+"F0.wireOp",EDGE,"E13.23.0.13"),sQuery(id+"F0.wireOp",EDGE,"E13.23.0.14"),sQuery(id+"F0.wireOp",EDGE,"E13.23.0.15"),sQuery(id+"F0.wireOp",EDGE,"E13.23.0.17"),sQuery(id+"F0.wireOp",EDGE,"E13.24.0.0"),sQuery(id+"F0.wireOp",EDGE,"E13.24.0.1"),sQuery(id+"F0.wireOp",EDGE,"E13.24.0.2"),sQuery(id+"F0.wireOp",EDGE,"E13.24.0.3"),sQuery(id+"F0.wireOp",EDGE,"E13.24.0.4"),sQuery(id+"F0.wireOp",EDGE,"E13.24.0.6"),sQuery(id+"F0.wireOp",EDGE,"E13.24.0.8"),sQuery(id+"F0.wireOp",EDGE,"E13.24.0.9"),sQuery(id+"F0.wireOp",EDGE,"E13.24.0.10"),sQuery(id+"F0.wireOp",EDGE,"E13.24.0.11"),sQuery(id+"F0.wireOp",EDGE,"E13.24.0.12"),sQuery(id+"F0.wireOp",EDGE,"E13.24.0.13"),sQuery(id+"F0.wireOp",EDGE,"E13.24.0.14"),sQuery(id+"F0.wireOp",EDGE,"E13.24.0.15"),sQuery(id+"F0.wireOp",EDGE,"E13.24.0.17"),sQuery(id+"F0.wireOp",EDGE,"E13.25.0.0"),sQuery(id+"F0.wireOp",EDGE,"E13.25.0.1"),sQuery(id+"F0.wireOp",EDGE,"E13.25.0.2"),sQuery(id+"F0.wireOp",EDGE,"E13.25.0.3"),sQuery(id+"F0.wireOp",EDGE,"E13.25.0.4"),sQuery(id+"F0.wireOp",EDGE,"E13.25.0.6"),sQuery(id+"F0.wireOp",EDGE,"E13.25.0.8"),sQuery(id+"F0.wireOp",EDGE,"E13.25.0.9"),sQuery(id+"F0.wireOp",EDGE,"E13.25.0.10"),sQuery(id+"F0.wireOp",EDGE,"E13.25.0.11"),sQuery(id+"F0.wireOp",EDGE,"E13.25.0.12"),sQuery(id+"F0.wireOp",EDGE,"E13.25.0.13"),sQuery(id+"F0.wireOp",EDGE,"E13.25.0.14"),sQuery(id+"F0.wireOp",EDGE,"E13.25.0.15"),sQuery(id+"F0.wireOp",EDGE,"E13.25.0.17"),sQuery(id+"F0.wireOp",EDGE,"E13.26.0.0"),sQuery(id+"F0.wireOp",EDGE,"E13.26.0.1"),sQuery(id+"F0.wireOp",EDGE,"E13.26.0.2"),sQuery(id+"F0.wireOp",EDGE,"E13.26.0.3"),sQuery(id+"F0.wireOp",EDGE,"E13.26.0.4"),sQuery(id+"F0.wireOp",EDGE,"E13.26.0.6"),sQuery(id+"F0.wireOp",EDGE,"E13.26.0.8"),sQuery(id+"F0.wireOp",EDGE,"E13.26.0.9"),sQuery(id+"F0.wireOp",EDGE,"E13.26.0.10"),sQuery(id+"F0.wireOp",EDGE,"E13.26.0.11"),sQuery(id+"F0.wireOp",EDGE,"E13.26.0.12"),sQuery(id+"F0.wireOp",EDGE,"E13.26.0.13"),sQuery(id+"F0.wireOp",EDGE,"E13.26.0.14"),sQuery(id+"F0.wireOp",EDGE,"E13.26.0.15"),sQuery(id+"F0.wireOp",EDGE,"E13.26.0.17"),sQuery(id+"F0.wireOp",EDGE,"E13.27.0.0"),sQuery(id+"F0.wireOp",EDGE,"E13.27.0.1"),sQuery(id+"F0.wireOp",EDGE,"E13.27.0.2"),sQuery(id+"F0.wireOp",EDGE,"E13.27.0.3"),sQuery(id+"F0.wireOp",EDGE,"E13.27.0.4"),sQuery(id+"F0.wireOp",EDGE,"E13.27.0.6"),sQuery(id+"F0.wireOp",EDGE,"E13.27.0.8"),sQuery(id+"F0.wireOp",EDGE,"E13.27.0.9"),sQuery(id+"F0.wireOp",EDGE,"E13.27.0.10"),sQuery(id+"F0.wireOp",EDGE,"E13.27.0.11"),sQuery(id+"F0.wireOp",EDGE,"E13.27.0.12"),sQuery(id+"F0.wireOp",EDGE,"E13.27.0.13"),sQuery(id+"F0.wireOp",EDGE,"E13.27.0.14"),sQuery(id+"F0.wireOp",EDGE,"E13.27.0.15"),sQuery(id+"F0.wireOp",EDGE,"E13.27.0.17")])],"isStart":true});
            var sketch = newSketch(context, id + "F2", { "sketchPlane" : qUnion([Q0])});
            skLineSegment(sketch, "E14.bottom", {"start": v(410.3, 190) * mm, "end": v(-5589.7, 190) * mm});
            skLineSegment(sketch, "E14.top", {"start": v(410.3, -2344.7) * mm, "end": v(-5589.7, -2344.7) * mm});
            skLineSegment(sketch, "E14.left", {"start": v(410.3, 190) * mm, "end": v(410.3, -2344.7) * mm});
            skLineSegment(sketch, "E14.right", {"start": v(-5589.7, 190) * mm, "end": v(-5589.7, -2344.7) * mm});
            skSolve(sketch);
        }
        {
            var Q0;
            Q0 = qSketchRegion(id + "F2", true);
            extrude(context, id + "F3", {"entities" : qUnion([Q0]), "operationType" : NewBodyOperationType.ADD, "depth" : 5 * mm});
        }
        {
            var Q0;
            Q0=makeQuery(id+"F1.opExtrude","CAP_FACE",FACE,{"disambiguationData":[OSD([sQuery(id+"F0.wireOp",EDGE,"E0"),sQuery(id+"F0.wireOp",EDGE,"E1"),sQuery(id+"F0.wireOp",EDGE,"E2"),sQuery(id+"F0.wireOp",EDGE,"E3"),sQuery(id+"F0.wireOp",EDGE,"E4.bottom"),sQuery(id+"F0.wireOp",EDGE,"E4.left"),sQuery(id+"F0.wireOp",EDGE,"E4.right"),sQuery(id+"F0.wireOp",EDGE,"E5.left"),sQuery(id+"F0.wireOp",EDGE,"E5.right"),sQuery(id+"F0.wireOp",EDGE,"E6.bottom"),sQuery(id+"F0.wireOp",EDGE,"E6.top"),sQuery(id+"F0.wireOp",EDGE,"E6.left"),sQuery(id+"F0.wireOp",EDGE,"E6.right"),sQuery(id+"F0.wireOp",EDGE,"E7.filletArc"),sQuery(id+"F0.wireOp",EDGE,"E8"),sQuery(id+"F0.wireOp",EDGE,"E9.filletArc"),sQuery(id+"F0.wireOp",EDGE,"E10.filletArc"),sQuery(id+"F0.wireOp",EDGE,"E11"),sQuery(id+"F0.wireOp",EDGE,"E12.filletArc"),sQuery(id+"F0.wireOp",EDGE,"E13.1.0.0"),sQuery(id+"F0.wireOp",EDGE,"E13.1.0.1"),sQuery(id+"F0.wireOp",EDGE,"E13.1.0.2"),sQuery(id+"F0.wireOp",EDGE,"E13.1.0.3"),sQuery(id+"F0.wireOp",EDGE,"E13.1.0.4"),sQuery(id+"F0.wireOp",EDGE,"E13.1.0.6"),sQuery(id+"F0.wireOp",EDGE,"E13.1.0.8"),sQuery(id+"F0.wireOp",EDGE,"E13.1.0.9"),sQuery(id+"F0.wireOp",EDGE,"E13.1.0.10"),sQuery(id+"F0.wireOp",EDGE,"E13.1.0.11"),sQuery(id+"F0.wireOp",EDGE,"E13.1.0.12"),sQuery(id+"F0.wireOp",EDGE,"E13.1.0.13"),sQuery(id+"F0.wireOp",EDGE,"E13.1.0.14"),sQuery(id+"F0.wireOp",EDGE,"E13.1.0.15"),sQuery(id+"F0.wireOp",EDGE,"E13.1.0.17"),sQuery(id+"F0.wireOp",EDGE,"E13.2.0.0"),sQuery(id+"F0.wireOp",EDGE,"E13.2.0.1"),sQuery(id+"F0.wireOp",EDGE,"E13.2.0.2"),sQuery(id+"F0.wireOp",EDGE,"E13.2.0.3"),sQuery(id+"F0.wireOp",EDGE,"E13.2.0.4"),sQuery(id+"F0.wireOp",EDGE,"E13.2.0.6"),sQuery(id+"F0.wireOp",EDGE,"E13.2.0.8"),sQuery(id+"F0.wireOp",EDGE,"E13.2.0.9"),sQuery(id+"F0.wireOp",EDGE,"E13.2.0.10"),sQuery(id+"F0.wireOp",EDGE,"E13.2.0.11"),sQuery(id+"F0.wireOp",EDGE,"E13.2.0.12"),sQuery(id+"F0.wireOp",EDGE,"E13.2.0.13"),sQuery(id+"F0.wireOp",EDGE,"E13.2.0.14"),sQuery(id+"F0.wireOp",EDGE,"E13.2.0.15"),sQuery(id+"F0.wireOp",EDGE,"E13.2.0.17"),sQuery(id+"F0.wireOp",EDGE,"E13.3.0.0"),sQuery(id+"F0.wireOp",EDGE,"E13.3.0.1"),sQuery(id+"F0.wireOp",EDGE,"E13.3.0.2"),sQuery(id+"F0.wireOp",EDGE,"E13.3.0.3"),sQuery(id+"F0.wireOp",EDGE,"E13.3.0.4"),sQuery(id+"F0.wireOp",EDGE,"E13.3.0.6"),sQuery(id+"F0.wireOp",EDGE,"E13.3.0.8"),sQuery(id+"F0.wireOp",EDGE,"E13.3.0.9"),sQuery(id+"F0.wireOp",EDGE,"E13.3.0.10"),sQuery(id+"F0.wireOp",EDGE,"E13.3.0.11"),sQuery(id+"F0.wireOp",EDGE,"E13.3.0.12"),sQuery(id+"F0.wireOp",EDGE,"E13.3.0.13"),sQuery(id+"F0.wireOp",EDGE,"E13.3.0.14"),sQuery(id+"F0.wireOp",EDGE,"E13.3.0.15"),sQuery(id+"F0.wireOp",EDGE,"E13.3.0.17"),sQuery(id+"F0.wireOp",EDGE,"E13.4.0.0"),sQuery(id+"F0.wireOp",EDGE,"E13.4.0.1"),sQuery(id+"F0.wireOp",EDGE,"E13.4.0.2"),sQuery(id+"F0.wireOp",EDGE,"E13.4.0.3"),sQuery(id+"F0.wireOp",EDGE,"E13.4.0.4"),sQuery(id+"F0.wireOp",EDGE,"E13.4.0.6"),sQuery(id+"F0.wireOp",EDGE,"E13.4.0.8"),sQuery(id+"F0.wireOp",EDGE,"E13.4.0.9"),sQuery(id+"F0.wireOp",EDGE,"E13.4.0.10"),sQuery(id+"F0.wireOp",EDGE,"E13.4.0.11"),sQuery(id+"F0.wireOp",EDGE,"E13.4.0.12"),sQuery(id+"F0.wireOp",EDGE,"E13.4.0.13"),sQuery(id+"F0.wireOp",EDGE,"E13.4.0.14"),sQuery(id+"F0.wireOp",EDGE,"E13.4.0.15"),sQuery(id+"F0.wireOp",EDGE,"E13.4.0.17"),sQuery(id+"F0.wireOp",EDGE,"E13.5.0.0"),sQuery(id+"F0.wireOp",EDGE,"E13.5.0.1"),sQuery(id+"F0.wireOp",EDGE,"E13.5.0.2"),sQuery(id+"F0.wireOp",EDGE,"E13.5.0.3"),sQuery(id+"F0.wireOp",EDGE,"E13.5.0.4"),sQuery(id+"F0.wireOp",EDGE,"E13.5.0.6"),sQuery(id+"F0.wireOp",EDGE,"E13.5.0.8"),sQuery(id+"F0.wireOp",EDGE,"E13.5.0.9"),sQuery(id+"F0.wireOp",EDGE,"E13.5.0.10"),sQuery(id+"F0.wireOp",EDGE,"E13.5.0.11"),sQuery(id+"F0.wireOp",EDGE,"E13.5.0.12"),sQuery(id+"F0.wireOp",EDGE,"E13.5.0.13"),sQuery(id+"F0.wireOp",EDGE,"E13.5.0.14"),sQuery(id+"F0.wireOp",EDGE,"E13.5.0.15"),sQuery(id+"F0.wireOp",EDGE,"E13.5.0.17"),sQuery(id+"F0.wireOp",EDGE,"E13.6.0.0"),sQuery(id+"F0.wireOp",EDGE,"E13.6.0.1"),sQuery(id+"F0.wireOp",EDGE,"E13.6.0.2"),sQuery(id+"F0.wireOp",EDGE,"E13.6.0.3"),sQuery(id+"F0.wireOp",EDGE,"E13.6.0.4"),sQuery(id+"F0.wireOp",EDGE,"E13.6.0.6"),sQuery(id+"F0.wireOp",EDGE,"E13.6.0.8"),sQuery(id+"F0.wireOp",EDGE,"E13.6.0.9"),sQuery(id+"F0.wireOp",EDGE,"E13.6.0.10"),sQuery(id+"F0.wireOp",EDGE,"E13.6.0.11"),sQuery(id+"F0.wireOp",EDGE,"E13.6.0.12"),sQuery(id+"F0.wireOp",EDGE,"E13.6.0.13"),sQuery(id+"F0.wireOp",EDGE,"E13.6.0.14"),sQuery(id+"F0.wireOp",EDGE,"E13.6.0.15"),sQuery(id+"F0.wireOp",EDGE,"E13.6.0.17"),sQuery(id+"F0.wireOp",EDGE,"E13.7.0.0"),sQuery(id+"F0.wireOp",EDGE,"E13.7.0.1"),sQuery(id+"F0.wireOp",EDGE,"E13.7.0.2"),sQuery(id+"F0.wireOp",EDGE,"E13.7.0.3"),sQuery(id+"F0.wireOp",EDGE,"E13.7.0.4"),sQuery(id+"F0.wireOp",EDGE,"E13.7.0.6"),sQuery(id+"F0.wireOp",EDGE,"E13.7.0.8"),sQuery(id+"F0.wireOp",EDGE,"E13.7.0.9"),sQuery(id+"F0.wireOp",EDGE,"E13.7.0.10"),sQuery(id+"F0.wireOp",EDGE,"E13.7.0.11"),sQuery(id+"F0.wireOp",EDGE,"E13.7.0.12"),sQuery(id+"F0.wireOp",EDGE,"E13.7.0.13"),sQuery(id+"F0.wireOp",EDGE,"E13.7.0.14"),sQuery(id+"F0.wireOp",EDGE,"E13.7.0.15"),sQuery(id+"F0.wireOp",EDGE,"E13.7.0.17"),sQuery(id+"F0.wireOp",EDGE,"E13.8.0.0"),sQuery(id+"F0.wireOp",EDGE,"E13.8.0.1"),sQuery(id+"F0.wireOp",EDGE,"E13.8.0.2"),sQuery(id+"F0.wireOp",EDGE,"E13.8.0.3"),sQuery(id+"F0.wireOp",EDGE,"E13.8.0.4"),sQuery(id+"F0.wireOp",EDGE,"E13.8.0.6"),sQuery(id+"F0.wireOp",EDGE,"E13.8.0.8"),sQuery(id+"F0.wireOp",EDGE,"E13.8.0.9"),sQuery(id+"F0.wireOp",EDGE,"E13.8.0.10"),sQuery(id+"F0.wireOp",EDGE,"E13.8.0.11"),sQuery(id+"F0.wireOp",EDGE,"E13.8.0.12"),sQuery(id+"F0.wireOp",EDGE,"E13.8.0.13"),sQuery(id+"F0.wireOp",EDGE,"E13.8.0.14"),sQuery(id+"F0.wireOp",EDGE,"E13.8.0.15"),sQuery(id+"F0.wireOp",EDGE,"E13.8.0.17"),sQuery(id+"F0.wireOp",EDGE,"E13.9.0.0"),sQuery(id+"F0.wireOp",EDGE,"E13.9.0.1"),sQuery(id+"F0.wireOp",EDGE,"E13.9.0.2"),sQuery(id+"F0.wireOp",EDGE,"E13.9.0.3"),sQuery(id+"F0.wireOp",EDGE,"E13.9.0.4"),sQuery(id+"F0.wireOp",EDGE,"E13.9.0.6"),sQuery(id+"F0.wireOp",EDGE,"E13.9.0.8"),sQuery(id+"F0.wireOp",EDGE,"E13.9.0.9"),sQuery(id+"F0.wireOp",EDGE,"E13.9.0.10"),sQuery(id+"F0.wireOp",EDGE,"E13.9.0.11"),sQuery(id+"F0.wireOp",EDGE,"E13.9.0.12"),sQuery(id+"F0.wireOp",EDGE,"E13.9.0.13"),sQuery(id+"F0.wireOp",EDGE,"E13.9.0.14"),sQuery(id+"F0.wireOp",EDGE,"E13.9.0.15"),sQuery(id+"F0.wireOp",EDGE,"E13.9.0.17"),sQuery(id+"F0.wireOp",EDGE,"E13.10.0.0"),sQuery(id+"F0.wireOp",EDGE,"E13.10.0.1"),sQuery(id+"F0.wireOp",EDGE,"E13.10.0.2"),sQuery(id+"F0.wireOp",EDGE,"E13.10.0.3"),sQuery(id+"F0.wireOp",EDGE,"E13.10.0.4"),sQuery(id+"F0.wireOp",EDGE,"E13.10.0.6"),sQuery(id+"F0.wireOp",EDGE,"E13.10.0.8"),sQuery(id+"F0.wireOp",EDGE,"E13.10.0.9"),sQuery(id+"F0.wireOp",EDGE,"E13.10.0.10"),sQuery(id+"F0.wireOp",EDGE,"E13.10.0.11"),sQuery(id+"F0.wireOp",EDGE,"E13.10.0.12"),sQuery(id+"F0.wireOp",EDGE,"E13.10.0.13"),sQuery(id+"F0.wireOp",EDGE,"E13.10.0.14"),sQuery(id+"F0.wireOp",EDGE,"E13.10.0.15"),sQuery(id+"F0.wireOp",EDGE,"E13.10.0.17"),sQuery(id+"F0.wireOp",EDGE,"E13.11.0.0"),sQuery(id+"F0.wireOp",EDGE,"E13.11.0.1"),sQuery(id+"F0.wireOp",EDGE,"E13.11.0.2"),sQuery(id+"F0.wireOp",EDGE,"E13.11.0.3"),sQuery(id+"F0.wireOp",EDGE,"E13.11.0.4"),sQuery(id+"F0.wireOp",EDGE,"E13.11.0.6"),sQuery(id+"F0.wireOp",EDGE,"E13.11.0.8"),sQuery(id+"F0.wireOp",EDGE,"E13.11.0.9"),sQuery(id+"F0.wireOp",EDGE,"E13.11.0.10"),sQuery(id+"F0.wireOp",EDGE,"E13.11.0.11"),sQuery(id+"F0.wireOp",EDGE,"E13.11.0.12"),sQuery(id+"F0.wireOp",EDGE,"E13.11.0.13"),sQuery(id+"F0.wireOp",EDGE,"E13.11.0.14"),sQuery(id+"F0.wireOp",EDGE,"E13.11.0.15"),sQuery(id+"F0.wireOp",EDGE,"E13.11.0.17"),sQuery(id+"F0.wireOp",EDGE,"E13.12.0.0"),sQuery(id+"F0.wireOp",EDGE,"E13.12.0.1"),sQuery(id+"F0.wireOp",EDGE,"E13.12.0.2"),sQuery(id+"F0.wireOp",EDGE,"E13.12.0.3"),sQuery(id+"F0.wireOp",EDGE,"E13.12.0.4"),sQuery(id+"F0.wireOp",EDGE,"E13.12.0.6"),sQuery(id+"F0.wireOp",EDGE,"E13.12.0.8"),sQuery(id+"F0.wireOp",EDGE,"E13.12.0.9"),sQuery(id+"F0.wireOp",EDGE,"E13.12.0.10"),sQuery(id+"F0.wireOp",EDGE,"E13.12.0.11"),sQuery(id+"F0.wireOp",EDGE,"E13.12.0.12"),sQuery(id+"F0.wireOp",EDGE,"E13.12.0.13"),sQuery(id+"F0.wireOp",EDGE,"E13.12.0.14"),sQuery(id+"F0.wireOp",EDGE,"E13.12.0.15"),sQuery(id+"F0.wireOp",EDGE,"E13.12.0.17"),sQuery(id+"F0.wireOp",EDGE,"E13.13.0.0"),sQuery(id+"F0.wireOp",EDGE,"E13.13.0.1"),sQuery(id+"F0.wireOp",EDGE,"E13.13.0.2"),sQuery(id+"F0.wireOp",EDGE,"E13.13.0.3"),sQuery(id+"F0.wireOp",EDGE,"E13.13.0.4"),sQuery(id+"F0.wireOp",EDGE,"E13.13.0.6"),sQuery(id+"F0.wireOp",EDGE,"E13.13.0.8"),sQuery(id+"F0.wireOp",EDGE,"E13.13.0.9"),sQuery(id+"F0.wireOp",EDGE,"E13.13.0.10"),sQuery(id+"F0.wireOp",EDGE,"E13.13.0.11"),sQuery(id+"F0.wireOp",EDGE,"E13.13.0.12"),sQuery(id+"F0.wireOp",EDGE,"E13.13.0.13"),sQuery(id+"F0.wireOp",EDGE,"E13.13.0.14"),sQuery(id+"F0.wireOp",EDGE,"E13.13.0.15"),sQuery(id+"F0.wireOp",EDGE,"E13.13.0.17"),sQuery(id+"F0.wireOp",EDGE,"E13.14.0.0"),sQuery(id+"F0.wireOp",EDGE,"E13.14.0.1"),sQuery(id+"F0.wireOp",EDGE,"E13.14.0.2"),sQuery(id+"F0.wireOp",EDGE,"E13.14.0.3"),sQuery(id+"F0.wireOp",EDGE,"E13.14.0.4"),sQuery(id+"F0.wireOp",EDGE,"E13.14.0.6"),sQuery(id+"F0.wireOp",EDGE,"E13.14.0.8"),sQuery(id+"F0.wireOp",EDGE,"E13.14.0.9"),sQuery(id+"F0.wireOp",EDGE,"E13.14.0.10"),sQuery(id+"F0.wireOp",EDGE,"E13.14.0.11"),sQuery(id+"F0.wireOp",EDGE,"E13.14.0.12"),sQuery(id+"F0.wireOp",EDGE,"E13.14.0.13"),sQuery(id+"F0.wireOp",EDGE,"E13.14.0.14"),sQuery(id+"F0.wireOp",EDGE,"E13.14.0.15"),sQuery(id+"F0.wireOp",EDGE,"E13.14.0.17"),sQuery(id+"F0.wireOp",EDGE,"E13.15.0.0"),sQuery(id+"F0.wireOp",EDGE,"E13.15.0.1"),sQuery(id+"F0.wireOp",EDGE,"E13.15.0.2"),sQuery(id+"F0.wireOp",EDGE,"E13.15.0.3"),sQuery(id+"F0.wireOp",EDGE,"E13.15.0.4"),sQuery(id+"F0.wireOp",EDGE,"E13.15.0.6"),sQuery(id+"F0.wireOp",EDGE,"E13.15.0.8"),sQuery(id+"F0.wireOp",EDGE,"E13.15.0.9"),sQuery(id+"F0.wireOp",EDGE,"E13.15.0.10"),sQuery(id+"F0.wireOp",EDGE,"E13.15.0.11"),sQuery(id+"F0.wireOp",EDGE,"E13.15.0.12"),sQuery(id+"F0.wireOp",EDGE,"E13.15.0.13"),sQuery(id+"F0.wireOp",EDGE,"E13.15.0.14"),sQuery(id+"F0.wireOp",EDGE,"E13.15.0.15"),sQuery(id+"F0.wireOp",EDGE,"E13.15.0.17"),sQuery(id+"F0.wireOp",EDGE,"E13.16.0.0"),sQuery(id+"F0.wireOp",EDGE,"E13.16.0.1"),sQuery(id+"F0.wireOp",EDGE,"E13.16.0.2"),sQuery(id+"F0.wireOp",EDGE,"E13.16.0.3"),sQuery(id+"F0.wireOp",EDGE,"E13.16.0.4"),sQuery(id+"F0.wireOp",EDGE,"E13.16.0.6"),sQuery(id+"F0.wireOp",EDGE,"E13.16.0.8"),sQuery(id+"F0.wireOp",EDGE,"E13.16.0.9"),sQuery(id+"F0.wireOp",EDGE,"E13.16.0.10"),sQuery(id+"F0.wireOp",EDGE,"E13.16.0.11"),sQuery(id+"F0.wireOp",EDGE,"E13.16.0.12"),sQuery(id+"F0.wireOp",EDGE,"E13.16.0.13"),sQuery(id+"F0.wireOp",EDGE,"E13.16.0.14"),sQuery(id+"F0.wireOp",EDGE,"E13.16.0.15"),sQuery(id+"F0.wireOp",EDGE,"E13.16.0.17"),sQuery(id+"F0.wireOp",EDGE,"E13.17.0.0"),sQuery(id+"F0.wireOp",EDGE,"E13.17.0.1"),sQuery(id+"F0.wireOp",EDGE,"E13.17.0.2"),sQuery(id+"F0.wireOp",EDGE,"E13.17.0.3"),sQuery(id+"F0.wireOp",EDGE,"E13.17.0.4"),sQuery(id+"F0.wireOp",EDGE,"E13.17.0.6"),sQuery(id+"F0.wireOp",EDGE,"E13.17.0.8"),sQuery(id+"F0.wireOp",EDGE,"E13.17.0.9"),sQuery(id+"F0.wireOp",EDGE,"E13.17.0.10"),sQuery(id+"F0.wireOp",EDGE,"E13.17.0.11"),sQuery(id+"F0.wireOp",EDGE,"E13.17.0.12"),sQuery(id+"F0.wireOp",EDGE,"E13.17.0.13"),sQuery(id+"F0.wireOp",EDGE,"E13.17.0.14"),sQuery(id+"F0.wireOp",EDGE,"E13.17.0.15"),sQuery(id+"F0.wireOp",EDGE,"E13.17.0.17"),sQuery(id+"F0.wireOp",EDGE,"E13.18.0.0"),sQuery(id+"F0.wireOp",EDGE,"E13.18.0.1"),sQuery(id+"F0.wireOp",EDGE,"E13.18.0.2"),sQuery(id+"F0.wireOp",EDGE,"E13.18.0.3"),sQuery(id+"F0.wireOp",EDGE,"E13.18.0.4"),sQuery(id+"F0.wireOp",EDGE,"E13.18.0.6"),sQuery(id+"F0.wireOp",EDGE,"E13.18.0.8"),sQuery(id+"F0.wireOp",EDGE,"E13.18.0.9"),sQuery(id+"F0.wireOp",EDGE,"E13.18.0.10"),sQuery(id+"F0.wireOp",EDGE,"E13.18.0.11"),sQuery(id+"F0.wireOp",EDGE,"E13.18.0.12"),sQuery(id+"F0.wireOp",EDGE,"E13.18.0.13"),sQuery(id+"F0.wireOp",EDGE,"E13.18.0.14"),sQuery(id+"F0.wireOp",EDGE,"E13.18.0.15"),sQuery(id+"F0.wireOp",EDGE,"E13.18.0.17"),sQuery(id+"F0.wireOp",EDGE,"E13.19.0.0"),sQuery(id+"F0.wireOp",EDGE,"E13.19.0.1"),sQuery(id+"F0.wireOp",EDGE,"E13.19.0.2"),sQuery(id+"F0.wireOp",EDGE,"E13.19.0.3"),sQuery(id+"F0.wireOp",EDGE,"E13.19.0.4"),sQuery(id+"F0.wireOp",EDGE,"E13.19.0.6"),sQuery(id+"F0.wireOp",EDGE,"E13.19.0.8"),sQuery(id+"F0.wireOp",EDGE,"E13.19.0.9"),sQuery(id+"F0.wireOp",EDGE,"E13.19.0.10"),sQuery(id+"F0.wireOp",EDGE,"E13.19.0.11"),sQuery(id+"F0.wireOp",EDGE,"E13.19.0.12"),sQuery(id+"F0.wireOp",EDGE,"E13.19.0.13"),sQuery(id+"F0.wireOp",EDGE,"E13.19.0.14"),sQuery(id+"F0.wireOp",EDGE,"E13.19.0.15"),sQuery(id+"F0.wireOp",EDGE,"E13.19.0.17"),sQuery(id+"F0.wireOp",EDGE,"E13.20.0.0"),sQuery(id+"F0.wireOp",EDGE,"E13.20.0.1"),sQuery(id+"F0.wireOp",EDGE,"E13.20.0.2"),sQuery(id+"F0.wireOp",EDGE,"E13.20.0.3"),sQuery(id+"F0.wireOp",EDGE,"E13.20.0.4"),sQuery(id+"F0.wireOp",EDGE,"E13.20.0.6"),sQuery(id+"F0.wireOp",EDGE,"E13.20.0.8"),sQuery(id+"F0.wireOp",EDGE,"E13.20.0.9"),sQuery(id+"F0.wireOp",EDGE,"E13.20.0.10"),sQuery(id+"F0.wireOp",EDGE,"E13.20.0.11"),sQuery(id+"F0.wireOp",EDGE,"E13.20.0.12"),sQuery(id+"F0.wireOp",EDGE,"E13.20.0.13"),sQuery(id+"F0.wireOp",EDGE,"E13.20.0.14"),sQuery(id+"F0.wireOp",EDGE,"E13.20.0.15"),sQuery(id+"F0.wireOp",EDGE,"E13.20.0.17"),sQuery(id+"F0.wireOp",EDGE,"E13.21.0.0"),sQuery(id+"F0.wireOp",EDGE,"E13.21.0.1"),sQuery(id+"F0.wireOp",EDGE,"E13.21.0.2"),sQuery(id+"F0.wireOp",EDGE,"E13.21.0.3"),sQuery(id+"F0.wireOp",EDGE,"E13.21.0.4"),sQuery(id+"F0.wireOp",EDGE,"E13.21.0.6"),sQuery(id+"F0.wireOp",EDGE,"E13.21.0.8"),sQuery(id+"F0.wireOp",EDGE,"E13.21.0.9"),sQuery(id+"F0.wireOp",EDGE,"E13.21.0.10"),sQuery(id+"F0.wireOp",EDGE,"E13.21.0.11"),sQuery(id+"F0.wireOp",EDGE,"E13.21.0.12"),sQuery(id+"F0.wireOp",EDGE,"E13.21.0.13"),sQuery(id+"F0.wireOp",EDGE,"E13.21.0.14"),sQuery(id+"F0.wireOp",EDGE,"E13.21.0.15"),sQuery(id+"F0.wireOp",EDGE,"E13.21.0.17"),sQuery(id+"F0.wireOp",EDGE,"E13.22.0.0"),sQuery(id+"F0.wireOp",EDGE,"E13.22.0.1"),sQuery(id+"F0.wireOp",EDGE,"E13.22.0.2"),sQuery(id+"F0.wireOp",EDGE,"E13.22.0.3"),sQuery(id+"F0.wireOp",EDGE,"E13.22.0.4"),sQuery(id+"F0.wireOp",EDGE,"E13.22.0.6"),sQuery(id+"F0.wireOp",EDGE,"E13.22.0.8"),sQuery(id+"F0.wireOp",EDGE,"E13.22.0.9"),sQuery(id+"F0.wireOp",EDGE,"E13.22.0.10"),sQuery(id+"F0.wireOp",EDGE,"E13.22.0.11"),sQuery(id+"F0.wireOp",EDGE,"E13.22.0.12"),sQuery(id+"F0.wireOp",EDGE,"E13.22.0.13"),sQuery(id+"F0.wireOp",EDGE,"E13.22.0.14"),sQuery(id+"F0.wireOp",EDGE,"E13.22.0.15"),sQuery(id+"F0.wireOp",EDGE,"E13.22.0.17"),sQuery(id+"F0.wireOp",EDGE,"E13.23.0.0"),sQuery(id+"F0.wireOp",EDGE,"E13.23.0.1"),sQuery(id+"F0.wireOp",EDGE,"E13.23.0.2"),sQuery(id+"F0.wireOp",EDGE,"E13.23.0.3"),sQuery(id+"F0.wireOp",EDGE,"E13.23.0.4"),sQuery(id+"F0.wireOp",EDGE,"E13.23.0.6"),sQuery(id+"F0.wireOp",EDGE,"E13.23.0.8"),sQuery(id+"F0.wireOp",EDGE,"E13.23.0.9"),sQuery(id+"F0.wireOp",EDGE,"E13.23.0.10"),sQuery(id+"F0.wireOp",EDGE,"E13.23.0.11"),sQuery(id+"F0.wireOp",EDGE,"E13.23.0.12"),sQuery(id+"F0.wireOp",EDGE,"E13.23.0.13"),sQuery(id+"F0.wireOp",EDGE,"E13.23.0.14"),sQuery(id+"F0.wireOp",EDGE,"E13.23.0.15"),sQuery(id+"F0.wireOp",EDGE,"E13.23.0.17"),sQuery(id+"F0.wireOp",EDGE,"E13.24.0.0"),sQuery(id+"F0.wireOp",EDGE,"E13.24.0.1"),sQuery(id+"F0.wireOp",EDGE,"E13.24.0.2"),sQuery(id+"F0.wireOp",EDGE,"E13.24.0.3"),sQuery(id+"F0.wireOp",EDGE,"E13.24.0.4"),sQuery(id+"F0.wireOp",EDGE,"E13.24.0.6"),sQuery(id+"F0.wireOp",EDGE,"E13.24.0.8"),sQuery(id+"F0.wireOp",EDGE,"E13.24.0.9"),sQuery(id+"F0.wireOp",EDGE,"E13.24.0.10"),sQuery(id+"F0.wireOp",EDGE,"E13.24.0.11"),sQuery(id+"F0.wireOp",EDGE,"E13.24.0.12"),sQuery(id+"F0.wireOp",EDGE,"E13.24.0.13"),sQuery(id+"F0.wireOp",EDGE,"E13.24.0.14"),sQuery(id+"F0.wireOp",EDGE,"E13.24.0.15"),sQuery(id+"F0.wireOp",EDGE,"E13.24.0.17"),sQuery(id+"F0.wireOp",EDGE,"E13.25.0.0"),sQuery(id+"F0.wireOp",EDGE,"E13.25.0.1"),sQuery(id+"F0.wireOp",EDGE,"E13.25.0.2"),sQuery(id+"F0.wireOp",EDGE,"E13.25.0.3"),sQuery(id+"F0.wireOp",EDGE,"E13.25.0.4"),sQuery(id+"F0.wireOp",EDGE,"E13.25.0.6"),sQuery(id+"F0.wireOp",EDGE,"E13.25.0.8"),sQuery(id+"F0.wireOp",EDGE,"E13.25.0.9"),sQuery(id+"F0.wireOp",EDGE,"E13.25.0.10"),sQuery(id+"F0.wireOp",EDGE,"E13.25.0.11"),sQuery(id+"F0.wireOp",EDGE,"E13.25.0.12"),sQuery(id+"F0.wireOp",EDGE,"E13.25.0.13"),sQuery(id+"F0.wireOp",EDGE,"E13.25.0.14"),sQuery(id+"F0.wireOp",EDGE,"E13.25.0.15"),sQuery(id+"F0.wireOp",EDGE,"E13.25.0.17"),sQuery(id+"F0.wireOp",EDGE,"E13.26.0.0"),sQuery(id+"F0.wireOp",EDGE,"E13.26.0.1"),sQuery(id+"F0.wireOp",EDGE,"E13.26.0.2"),sQuery(id+"F0.wireOp",EDGE,"E13.26.0.3"),sQuery(id+"F0.wireOp",EDGE,"E13.26.0.4"),sQuery(id+"F0.wireOp",EDGE,"E13.26.0.6"),sQuery(id+"F0.wireOp",EDGE,"E13.26.0.8"),sQuery(id+"F0.wireOp",EDGE,"E13.26.0.9"),sQuery(id+"F0.wireOp",EDGE,"E13.26.0.10"),sQuery(id+"F0.wireOp",EDGE,"E13.26.0.11"),sQuery(id+"F0.wireOp",EDGE,"E13.26.0.12"),sQuery(id+"F0.wireOp",EDGE,"E13.26.0.13"),sQuery(id+"F0.wireOp",EDGE,"E13.26.0.14"),sQuery(id+"F0.wireOp",EDGE,"E13.26.0.15"),sQuery(id+"F0.wireOp",EDGE,"E13.26.0.17"),sQuery(id+"F0.wireOp",EDGE,"E13.27.0.0"),sQuery(id+"F0.wireOp",EDGE,"E13.27.0.1"),sQuery(id+"F0.wireOp",EDGE,"E13.27.0.2"),sQuery(id+"F0.wireOp",EDGE,"E13.27.0.3"),sQuery(id+"F0.wireOp",EDGE,"E13.27.0.4"),sQuery(id+"F0.wireOp",EDGE,"E13.27.0.6"),sQuery(id+"F0.wireOp",EDGE,"E13.27.0.8"),sQuery(id+"F0.wireOp",EDGE,"E13.27.0.9"),sQuery(id+"F0.wireOp",EDGE,"E13.27.0.10"),sQuery(id+"F0.wireOp",EDGE,"E13.27.0.11"),sQuery(id+"F0.wireOp",EDGE,"E13.27.0.12"),sQuery(id+"F0.wireOp",EDGE,"E13.27.0.13"),sQuery(id+"F0.wireOp",EDGE,"E13.27.0.14"),sQuery(id+"F0.wireOp",EDGE,"E13.27.0.15"),sQuery(id+"F0.wireOp",EDGE,"E13.27.0.17")])],"isStart":false});
            var sketch = newSketch(context, id + "F4", { "sketchPlane" : qUnion([Q0])});
            skLineSegment(sketch, "E15.bottom", {"start": v(-410.3, 190) * mm, "end": v(5589.7, 190) * mm});
            skLineSegment(sketch, "E15.top", {"start": v(-410.3, -2344.7) * mm, "end": v(5589.7, -2344.7) * mm});
            skLineSegment(sketch, "E15.left", {"start": v(-410.3, 190) * mm, "end": v(-410.3, -2344.7) * mm});
            skLineSegment(sketch, "E15.right", {"start": v(5589.7, 190) * mm, "end": v(5589.7, -2344.7) * mm});
            skSolve(sketch);
        }
        {
            var Q0;
            Q0 = qSketchRegion(id + "F4", true);
            extrude(context, id + "F5", {"entities" : qUnion([Q0]), "operationType" : NewBodyOperationType.ADD, "depth" : 5 * mm});
        }
        {
            var Q0;
            Q0=makeQuery(id+"F5.boolean.opBoolean","MERGE",FACE,{"derivedFrom":[makeQuery(id+"F3.boolean.opBoolean","MERGE",FACE,{"derivedFrom":[makeQuery(id+"F1.opExtrude","SWEPT_FACE",FACE,{"disambiguationData":[OSD([sQuery(id+"F0.wireOp",EDGE,"E1"),sQuery(id+"F0.wireOp",EDGE,"E13.10.0.17")])]}),makeQuery(id+"F1.opExtrude","SWEPT_FACE",FACE,{"disambiguationData":[OSD([sQuery(id+"F0.wireOp",EDGE,"E13.10.0.13")])]}),makeQuery(id+"F3.opExtrude","SWEPT_FACE",FACE,{"disambiguationData":[OSD([sQuery(id+"F2.wireOp",EDGE,"E14.right")])]})]}),makeQuery(id+"F5.opExtrude","SWEPT_FACE",FACE,{"disambiguationData":[OSD([sQuery(id+"F4.wireOp",EDGE,"E15.right")])]})]});
            var sketch = newSketch(context, id + "F6", { "sketchPlane" : qUnion([Q0])});
            skLineSegment(sketch, "E16", {"start": v(-2460.67, 190) * mm, "end": v(-2460.67, 290) * mm});
            skLineSegment(sketch, "E17", {"start": v(-2460.67, 290) * mm, "end": v(-2455.67, 290) * mm});
            skLineSegment(sketch, "E18", {"start": v(-2455.67, 290) * mm, "end": v(-2455.67, 190) * mm});
            skLineSegment(sketch, "E19", {"start": v(-2455.67, 190) * mm, "end": v(-2460.67, 190) * mm});
            skLineSegment(sketch, "E20.1.0.0", {"start": v(-2285.67, 290) * mm, "end": v(-2285.67, 190) * mm});
            skLineSegment(sketch, "E20.1.0.1", {"start": v(-2290.67, 290) * mm, "end": v(-2285.67, 290) * mm});
            skLineSegment(sketch, "E20.1.0.2", {"start": v(-2290.67, 190) * mm, "end": v(-2290.67, 290) * mm});
            skLineSegment(sketch, "E20.1.0.3", {"start": v(-2285.67, 190) * mm, "end": v(-2290.67, 190) * mm});
            skLineSegment(sketch, "E20.2.0.0", {"start": v(-2115.67, 290) * mm, "end": v(-2115.67, 190) * mm});
            skLineSegment(sketch, "E20.2.0.1", {"start": v(-2120.67, 290) * mm, "end": v(-2115.67, 290) * mm});
            skLineSegment(sketch, "E20.2.0.2", {"start": v(-2120.67, 190) * mm, "end": v(-2120.67, 290) * mm});
            skLineSegment(sketch, "E20.2.0.3", {"start": v(-2115.67, 190) * mm, "end": v(-2120.67, 190) * mm});
            skLineSegment(sketch, "E20.3.0.0", {"start": v(-1945.67, 290) * mm, "end": v(-1945.67, 190) * mm});
            skLineSegment(sketch, "E20.3.0.1", {"start": v(-1950.67, 290) * mm, "end": v(-1945.67, 290) * mm});
            skLineSegment(sketch, "E20.3.0.2", {"start": v(-1950.67, 190) * mm, "end": v(-1950.67, 290) * mm});
            skLineSegment(sketch, "E20.3.0.3", {"start": v(-1945.67, 190) * mm, "end": v(-1950.67, 190) * mm});
            skLineSegment(sketch, "E20.4.0.0", {"start": v(-1775.67, 290) * mm, "end": v(-1775.67, 190) * mm});
            skLineSegment(sketch, "E20.4.0.1", {"start": v(-1780.67, 290) * mm, "end": v(-1775.67, 290) * mm});
            skLineSegment(sketch, "E20.4.0.2", {"start": v(-1780.67, 190) * mm, "end": v(-1780.67, 290) * mm});
            skLineSegment(sketch, "E20.4.0.3", {"start": v(-1775.67, 190) * mm, "end": v(-1780.67, 190) * mm});
            skLineSegment(sketch, "E20.5.0.0", {"start": v(-1605.67, 290) * mm, "end": v(-1605.67, 190) * mm});
            skLineSegment(sketch, "E20.5.0.1", {"start": v(-1610.67, 290) * mm, "end": v(-1605.67, 290) * mm});
            skLineSegment(sketch, "E20.5.0.2", {"start": v(-1610.67, 190) * mm, "end": v(-1610.67, 290) * mm});
            skLineSegment(sketch, "E20.5.0.3", {"start": v(-1605.67, 190) * mm, "end": v(-1610.67, 190) * mm});
            skLineSegment(sketch, "E20.6.0.0", {"start": v(-1435.67, 290) * mm, "end": v(-1435.67, 190) * mm});
            skLineSegment(sketch, "E20.6.0.1", {"start": v(-1440.67, 290) * mm, "end": v(-1435.67, 290) * mm});
            skLineSegment(sketch, "E20.6.0.2", {"start": v(-1440.67, 190) * mm, "end": v(-1440.67, 290) * mm});
            skLineSegment(sketch, "E20.6.0.3", {"start": v(-1435.67, 190) * mm, "end": v(-1440.67, 190) * mm});
            skLineSegment(sketch, "E20.7.0.0", {"start": v(-1265.67, 290) * mm, "end": v(-1265.67, 190) * mm});
            skLineSegment(sketch, "E20.7.0.1", {"start": v(-1270.67, 290) * mm, "end": v(-1265.67, 290) * mm});
            skLineSegment(sketch, "E20.7.0.2", {"start": v(-1270.67, 190) * mm, "end": v(-1270.67, 290) * mm});
            skLineSegment(sketch, "E20.7.0.3", {"start": v(-1265.67, 190) * mm, "end": v(-1270.67, 190) * mm});
            skLineSegment(sketch, "E20.8.0.0", {"start": v(-1095.67, 290) * mm, "end": v(-1095.67, 190) * mm});
            skLineSegment(sketch, "E20.8.0.1", {"start": v(-1100.67, 290) * mm, "end": v(-1095.67, 290) * mm});
            skLineSegment(sketch, "E20.8.0.2", {"start": v(-1100.67, 190) * mm, "end": v(-1100.67, 290) * mm});
            skLineSegment(sketch, "E20.8.0.3", {"start": v(-1095.67, 190) * mm, "end": v(-1100.67, 190) * mm});
            skLineSegment(sketch, "E20.9.0.0", {"start": v(-925.67, 290) * mm, "end": v(-925.67, 190) * mm});
            skLineSegment(sketch, "E20.9.0.1", {"start": v(-930.67, 290) * mm, "end": v(-925.67, 290) * mm});
            skLineSegment(sketch, "E20.9.0.2", {"start": v(-930.67, 190) * mm, "end": v(-930.67, 290) * mm});
            skLineSegment(sketch, "E20.9.0.3", {"start": v(-925.67, 190) * mm, "end": v(-930.67, 190) * mm});
            skLineSegment(sketch, "E20.10.0.0", {"start": v(-755.67, 290) * mm, "end": v(-755.67, 190) * mm});
            skLineSegment(sketch, "E20.10.0.1", {"start": v(-760.67, 290) * mm, "end": v(-755.67, 290) * mm});
            skLineSegment(sketch, "E20.10.0.2", {"start": v(-760.67, 190) * mm, "end": v(-760.67, 290) * mm});
            skLineSegment(sketch, "E20.10.0.3", {"start": v(-755.67, 190) * mm, "end": v(-760.67, 190) * mm});
            skLineSegment(sketch, "E20.11.0.0", {"start": v(-585.67, 290) * mm, "end": v(-585.67, 190) * mm});
            skLineSegment(sketch, "E20.11.0.1", {"start": v(-590.67, 290) * mm, "end": v(-585.67, 290) * mm});
            skLineSegment(sketch, "E20.11.0.2", {"start": v(-590.67, 190) * mm, "end": v(-590.67, 290) * mm});
            skLineSegment(sketch, "E20.11.0.3", {"start": v(-585.67, 190) * mm, "end": v(-590.67, 190) * mm});
            skLineSegment(sketch, "E20.12.0.0", {"start": v(-415.67, 290) * mm, "end": v(-415.67, 190) * mm});
            skLineSegment(sketch, "E20.12.0.1", {"start": v(-420.67, 290) * mm, "end": v(-415.67, 290) * mm});
            skLineSegment(sketch, "E20.12.0.2", {"start": v(-420.67, 190) * mm, "end": v(-420.67, 290) * mm});
            skLineSegment(sketch, "E20.12.0.3", {"start": v(-415.67, 190) * mm, "end": v(-420.67, 190) * mm});
            skLineSegment(sketch, "E20.13.0.0", {"start": v(-245.67, 290) * mm, "end": v(-245.67, 190) * mm});
            skLineSegment(sketch, "E20.13.0.1", {"start": v(-250.67, 290) * mm, "end": v(-245.67, 290) * mm});
            skLineSegment(sketch, "E20.13.0.2", {"start": v(-250.67, 190) * mm, "end": v(-250.67, 290) * mm});
            skLineSegment(sketch, "E20.13.0.3", {"start": v(-245.67, 190) * mm, "end": v(-250.67, 190) * mm});
            skLineSegment(sketch, "E20.14.0.0", {"start": v(-75.67, 290) * mm, "end": v(-75.67, 190) * mm});
            skLineSegment(sketch, "E20.14.0.1", {"start": v(-80.67, 290) * mm, "end": v(-75.67, 290) * mm});
            skLineSegment(sketch, "E20.14.0.2", {"start": v(-80.67, 190) * mm, "end": v(-80.67, 290) * mm});
            skLineSegment(sketch, "E20.14.0.3", {"start": v(-75.67, 190) * mm, "end": v(-80.67, 190) * mm});
            skLineSegment(sketch, "E20.direction1", {"start": v(-2460.67, 190) * mm, "end": v(-2290.67, 190) * mm, "construction": true});
            skLineSegment(sketch, "E21", {"start": v(-2503.83, 290) * mm, "end": v(0, 290) * mm});
            skLineSegment(sketch, "E22", {"start": v(0, 290) * mm, "end": v(0, 295) * mm});
            skLineSegment(sketch, "E23", {"start": v(0, 295) * mm, "end": v(-2503.83, 295) * mm});
            skLineSegment(sketch, "E24", {"start": v(-2503.83, 295) * mm, "end": v(-2503.83, 290) * mm});
            skSolve(sketch);
        }
        {
            var Q0;
            Q0 = qSketchRegion(id + "F6", true);
            extrude(context, id + "F7", {"entities" : qUnion([Q0]), "oppositeDirection" : true, "depth" : 6000 * mm});
        }
    });
